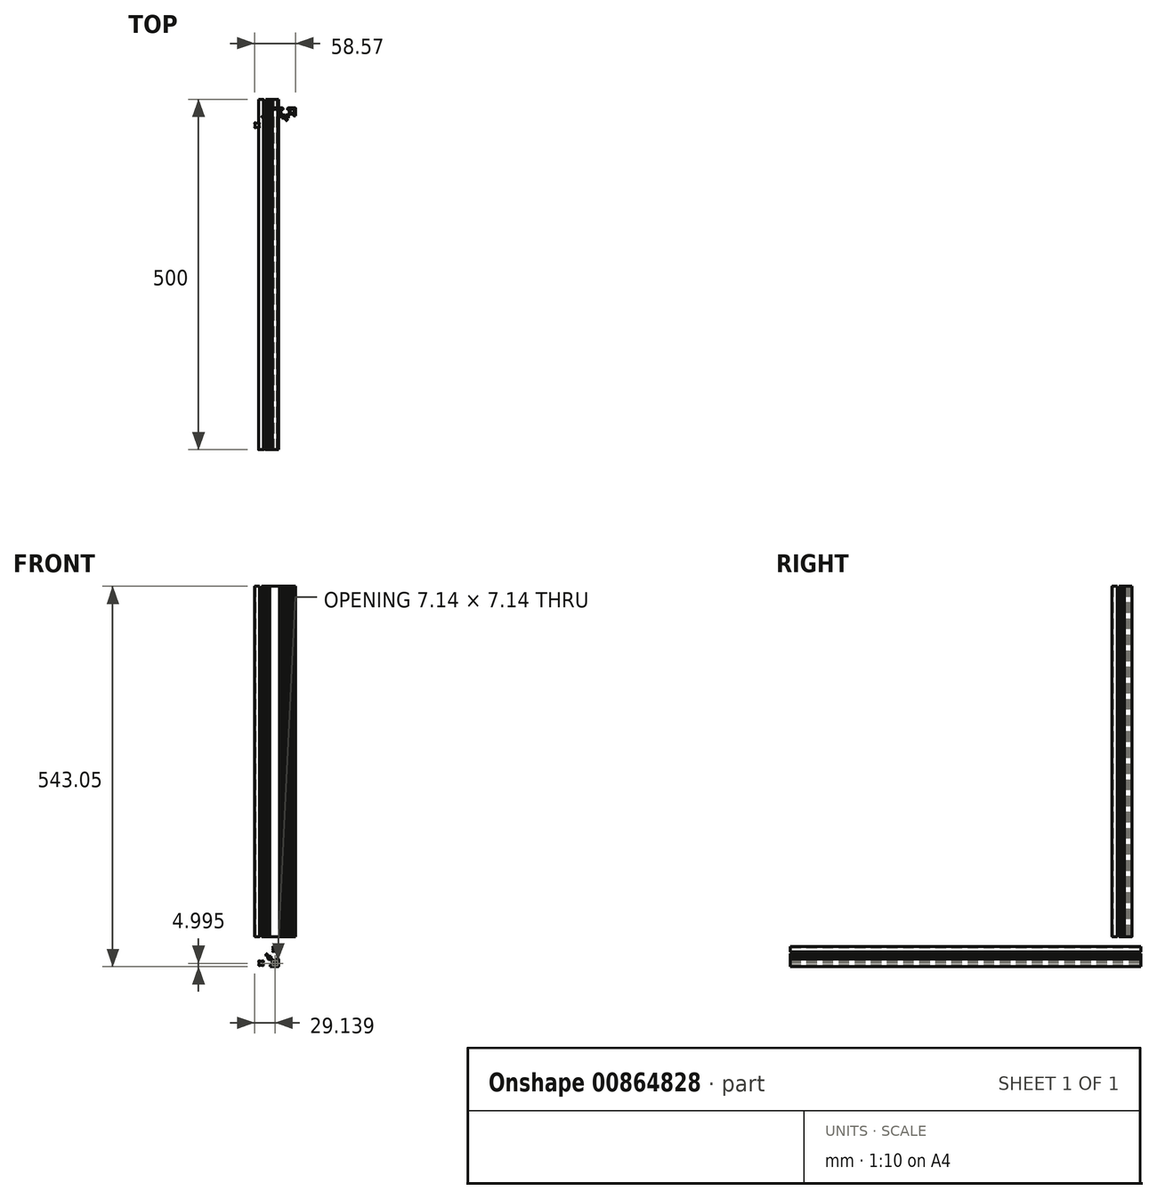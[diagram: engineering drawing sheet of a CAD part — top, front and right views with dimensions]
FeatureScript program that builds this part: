
annotation { "Feature Type Name" : "Feature", "Feature Type Description" : "" }
export const myFeature = defineFeature(function(context is Context, id is Id, definition is map)
    precondition{}
    {
        {
            var Q0;
            Q0=qCreatedBy(makeId("Top.planeOp"),FACE);
            var sketch = newSketch(context, id + "F0", { "sketchPlane" : qUnion([Q0])});
            skArc(sketch, "E0", {"start": v(-25.7, -35.74) * mm, "mid": v(-25.73, -35.56) * mm, "end": v(-25.65, -35.4) * mm});
            skLineSegment(sketch, "E1", {"start": v(-25.65, -35.4) * mm, "end": v(-24.9, -34.66) * mm});
            skArc(sketch, "E2", {"start": v(-24.9, -34.66) * mm, "mid": v(-24.82, -34.46) * mm, "end": v(-24.88, -34.26) * mm});
            skArc(sketch, "E3", {"start": v(-24.88, -34.26) * mm, "mid": v(-25.2, -33.9) * mm, "end": v(-25.57, -33.58) * mm});
            skArc(sketch, "E4", {"start": v(-25.57, -33.58) * mm, "mid": v(-25.77, -33.51) * mm, "end": v(-25.97, -33.6) * mm});
            skLineSegment(sketch, "E5", {"start": v(-25.97, -33.6) * mm, "end": v(-26.7, -34.34) * mm});
            skArc(sketch, "E6", {"start": v(-26.7, -34.34) * mm, "mid": v(-26.87, -34.42) * mm, "end": v(-27.05, -34.4) * mm});
            skArc(sketch, "E7", {"start": v(-27.05, -34.4) * mm, "mid": v(-28.39, -34.08) * mm, "end": v(-29.72, -34.4) * mm});
            skArc(sketch, "E8", {"start": v(-29.72, -34.4) * mm, "mid": v(-29.9, -34.42) * mm, "end": v(-30.07, -34.34) * mm});
            skLineSegment(sketch, "E9", {"start": v(-30.07, -34.34) * mm, "end": v(-30.81, -33.6) * mm});
            skArc(sketch, "E10", {"start": v(-30.81, -33.6) * mm, "mid": v(-31, -33.51) * mm, "end": v(-31.21, -33.58) * mm});
            skArc(sketch, "E11", {"start": v(-31.21, -33.58) * mm, "mid": v(-31.57, -33.9) * mm, "end": v(-31.9, -34.26) * mm});
            skArc(sketch, "E12", {"start": v(-31.9, -34.26) * mm, "mid": v(-31.96, -34.46) * mm, "end": v(-31.87, -34.66) * mm});
            skLineSegment(sketch, "E13", {"start": v(-31.87, -34.66) * mm, "end": v(-31.13, -35.4) * mm});
            skArc(sketch, "E14", {"start": v(-31.13, -35.4) * mm, "mid": v(-31.05, -35.56) * mm, "end": v(-31.07, -35.75) * mm});
            skArc(sketch, "E15", {"start": v(-31.07, -35.75) * mm, "mid": v(-31.39, -37.08) * mm, "end": v(-31.07, -38.42) * mm});
            skArc(sketch, "E16", {"start": v(-31.07, -38.42) * mm, "mid": v(-31.05, -38.6) * mm, "end": v(-31.13, -38.76) * mm});
            skLineSegment(sketch, "E17", {"start": v(-31.13, -38.76) * mm, "end": v(-31.87, -39.5) * mm});
            skArc(sketch, "E18", {"start": v(-31.87, -39.5) * mm, "mid": v(-31.96, -39.7) * mm, "end": v(-31.9, -39.9) * mm});
            skArc(sketch, "E19", {"start": v(-31.9, -39.9) * mm, "mid": v(-31.57, -40.26) * mm, "end": v(-31.21, -40.59) * mm});
            skArc(sketch, "E20", {"start": v(-31.21, -40.59) * mm, "mid": v(-31, -40.65) * mm, "end": v(-30.81, -40.56) * mm});
            skLineSegment(sketch, "E21", {"start": v(-30.81, -40.56) * mm, "end": v(-30.07, -39.82) * mm});
            skArc(sketch, "E22", {"start": v(-30.07, -39.82) * mm, "mid": v(-29.9, -39.74) * mm, "end": v(-29.72, -39.77) * mm});
            skArc(sketch, "E23", {"start": v(-29.72, -39.77) * mm, "mid": v(-28.39, -40.08) * mm, "end": v(-27.05, -39.77) * mm});
            skArc(sketch, "E24", {"start": v(-27.05, -39.77) * mm, "mid": v(-26.87, -39.74) * mm, "end": v(-26.7, -39.82) * mm});
            skLineSegment(sketch, "E25", {"start": v(-26.7, -39.82) * mm, "end": v(-25.97, -40.56) * mm});
            skArc(sketch, "E26", {"start": v(-25.97, -40.56) * mm, "mid": v(-25.77, -40.65) * mm, "end": v(-25.57, -40.59) * mm});
            skArc(sketch, "E27", {"start": v(-25.57, -40.59) * mm, "mid": v(-25.2, -40.26) * mm, "end": v(-24.88, -39.9) * mm});
            skArc(sketch, "E28", {"start": v(-24.88, -39.9) * mm, "mid": v(-24.82, -39.7) * mm, "end": v(-24.9, -39.5) * mm});
            skLineSegment(sketch, "E29", {"start": v(-24.9, -39.5) * mm, "end": v(-25.65, -38.76) * mm});
            skArc(sketch, "E30", {"start": v(-25.65, -38.76) * mm, "mid": v(-25.73, -38.6) * mm, "end": v(-25.7, -38.42) * mm});
            skArc(sketch, "E31", {"start": v(-25.7, -38.42) * mm, "mid": v(-25.39, -37.08) * mm, "end": v(-25.7, -35.74) * mm});
            skLineSegment(sketch, "E32", {"start": v(-28.39, -34.88) * mm, "end": v(-28.39, -39.28) * mm});
            skLineSegment(sketch, "E33", {"start": v(-26.19, -37.08) * mm, "end": v(-30.59, -37.08) * mm});
            skLineSegment(sketch, "E34", {"start": v(-26.19, -17.08) * mm, "end": v(-30.59, -17.08) * mm});
            skLineSegment(sketch, "E35", {"start": v(-28.39, -19.28) * mm, "end": v(-28.39, -14.88) * mm});
            skLineSegment(sketch, "E36", {"start": v(28.01, -27.08) * mm, "end": v(-34.9, -27.08) * mm});
            skLineSegment(sketch, "E37", {"start": v(-18.39, -43.65) * mm, "end": v(-18.39, -10.92) * mm});
            skArc(sketch, "E38", {"start": v(-15.15, -25.5) * mm, "mid": v(-14.93, -25.32) * mm, "end": v(-14.95, -25.05) * mm});
            skArc(sketch, "E39", {"start": v(-14.95, -25.05) * mm, "mid": v(-15.56, -24.25) * mm, "end": v(-16.36, -23.64) * mm});
            skArc(sketch, "E40", {"start": v(-16.36, -23.64) * mm, "mid": v(-16.63, -23.62) * mm, "end": v(-16.8, -23.84) * mm});
            skLineSegment(sketch, "E41", {"start": v(-16.8, -23.84) * mm, "end": v(-16.94, -24.58) * mm});
            skArc(sketch, "E42", {"start": v(-16.94, -24.58) * mm, "mid": v(-17.1, -24.8) * mm, "end": v(-17.36, -24.8) * mm});
            skArc(sketch, "E43", {"start": v(-17.36, -24.8) * mm, "mid": v(-18.39, -24.58) * mm, "end": v(-19.42, -24.8) * mm});
            skArc(sketch, "E44", {"start": v(-19.42, -24.8) * mm, "mid": v(-19.69, -24.8) * mm, "end": v(-19.84, -24.58) * mm});
            skLineSegment(sketch, "E45", {"start": v(-19.84, -24.58) * mm, "end": v(-19.98, -23.84) * mm});
            skArc(sketch, "E46", {"start": v(-19.98, -23.84) * mm, "mid": v(-20.15, -23.62) * mm, "end": v(-20.42, -23.64) * mm});
            skArc(sketch, "E47", {"start": v(-20.42, -23.64) * mm, "mid": v(-21.22, -24.25) * mm, "end": v(-21.83, -25.05) * mm});
            skArc(sketch, "E48", {"start": v(-21.83, -25.05) * mm, "mid": v(-21.85, -25.32) * mm, "end": v(-21.63, -25.5) * mm});
            skLineSegment(sketch, "E49", {"start": v(-21.63, -25.5) * mm, "end": v(-20.89, -25.63) * mm});
            skArc(sketch, "E50", {"start": v(-20.89, -25.63) * mm, "mid": v(-20.67, -25.78) * mm, "end": v(-20.67, -26.05) * mm});
            skArc(sketch, "E51", {"start": v(-20.67, -26.05) * mm, "mid": v(-20.89, -27.08) * mm, "end": v(-20.67, -28.11) * mm});
            skArc(sketch, "E52", {"start": v(-20.67, -28.11) * mm, "mid": v(-20.67, -28.38) * mm, "end": v(-20.89, -28.53) * mm});
            skLineSegment(sketch, "E53", {"start": v(-20.89, -28.53) * mm, "end": v(-21.63, -28.67) * mm});
            skArc(sketch, "E54", {"start": v(-21.63, -28.67) * mm, "mid": v(-21.85, -28.84) * mm, "end": v(-21.83, -29.11) * mm});
            skArc(sketch, "E55", {"start": v(-21.83, -29.11) * mm, "mid": v(-21.22, -29.9) * mm, "end": v(-20.42, -30.52) * mm});
            skArc(sketch, "E56", {"start": v(-20.42, -30.52) * mm, "mid": v(-20.15, -30.54) * mm, "end": v(-19.98, -30.32) * mm});
            skLineSegment(sketch, "E57", {"start": v(-19.98, -30.32) * mm, "end": v(-19.84, -29.58) * mm});
            skArc(sketch, "E58", {"start": v(-19.84, -29.58) * mm, "mid": v(-19.69, -29.36) * mm, "end": v(-19.42, -29.36) * mm});
            skArc(sketch, "E59", {"start": v(-19.42, -29.36) * mm, "mid": v(-18.39, -29.58) * mm, "end": v(-17.36, -29.36) * mm});
            skArc(sketch, "E60", {"start": v(-17.36, -29.36) * mm, "mid": v(-17.1, -29.36) * mm, "end": v(-16.94, -29.58) * mm});
            skLineSegment(sketch, "E61", {"start": v(-16.94, -29.58) * mm, "end": v(-16.8, -30.32) * mm});
            skArc(sketch, "E62", {"start": v(-16.8, -30.32) * mm, "mid": v(-16.63, -30.54) * mm, "end": v(-16.36, -30.52) * mm});
            skArc(sketch, "E63", {"start": v(-16.36, -30.52) * mm, "mid": v(-15.56, -29.9) * mm, "end": v(-14.95, -29.11) * mm});
            skArc(sketch, "E64", {"start": v(-14.95, -29.11) * mm, "mid": v(-14.93, -28.84) * mm, "end": v(-15.15, -28.67) * mm});
            skLineSegment(sketch, "E65", {"start": v(-15.15, -28.67) * mm, "end": v(-15.9, -28.53) * mm});
            skArc(sketch, "E66", {"start": v(-15.9, -28.53) * mm, "mid": v(-16.1, -28.38) * mm, "end": v(-16.11, -28.11) * mm});
            skArc(sketch, "E67", {"start": v(-16.11, -28.11) * mm, "mid": v(-15.89, -27.08) * mm, "end": v(-16.11, -26.05) * mm});
            skArc(sketch, "E68", {"start": v(-16.11, -26.05) * mm, "mid": v(-16.1, -25.78) * mm, "end": v(-15.9, -25.63) * mm});
            skLineSegment(sketch, "E69", {"start": v(-15.9, -25.63) * mm, "end": v(-15.15, -25.5) * mm});
            skArc(sketch, "E70", {"start": v(-25.7, -18.42) * mm, "mid": v(-25.73, -18.6) * mm, "end": v(-25.65, -18.76) * mm});
            skLineSegment(sketch, "E71", {"start": v(-25.65, -18.76) * mm, "end": v(-24.9, -19.5) * mm});
            skArc(sketch, "E72", {"start": v(-24.9, -19.5) * mm, "mid": v(-24.82, -19.7) * mm, "end": v(-24.88, -19.9) * mm});
            skArc(sketch, "E73", {"start": v(-24.88, -19.9) * mm, "mid": v(-25.2, -20.26) * mm, "end": v(-25.57, -20.59) * mm});
            skArc(sketch, "E74", {"start": v(-25.57, -20.59) * mm, "mid": v(-25.77, -20.65) * mm, "end": v(-25.97, -20.56) * mm});
            skLineSegment(sketch, "E75", {"start": v(-25.97, -20.56) * mm, "end": v(-26.7, -19.82) * mm});
            skArc(sketch, "E76", {"start": v(-26.7, -19.82) * mm, "mid": v(-26.87, -19.74) * mm, "end": v(-27.05, -19.77) * mm});
            skArc(sketch, "E77", {"start": v(-27.05, -19.77) * mm, "mid": v(-28.39, -20.08) * mm, "end": v(-29.73, -19.77) * mm});
            skArc(sketch, "E78", {"start": v(-29.73, -19.77) * mm, "mid": v(-29.9, -19.74) * mm, "end": v(-30.07, -19.82) * mm});
            skLineSegment(sketch, "E79", {"start": v(-30.07, -19.82) * mm, "end": v(-30.81, -20.56) * mm});
            skArc(sketch, "E80", {"start": v(-30.81, -20.56) * mm, "mid": v(-31, -20.65) * mm, "end": v(-31.21, -20.59) * mm});
            skArc(sketch, "E81", {"start": v(-31.21, -20.59) * mm, "mid": v(-31.57, -20.26) * mm, "end": v(-31.9, -19.9) * mm});
            skArc(sketch, "E82", {"start": v(-31.9, -19.9) * mm, "mid": v(-31.96, -19.7) * mm, "end": v(-31.87, -19.5) * mm});
            skLineSegment(sketch, "E83", {"start": v(-31.87, -19.5) * mm, "end": v(-31.13, -18.76) * mm});
            skArc(sketch, "E84", {"start": v(-31.13, -18.76) * mm, "mid": v(-31.05, -18.6) * mm, "end": v(-31.08, -18.42) * mm});
            skArc(sketch, "E85", {"start": v(-31.08, -18.42) * mm, "mid": v(-31.39, -17.08) * mm, "end": v(-31.08, -15.74) * mm});
            skArc(sketch, "E86", {"start": v(-31.08, -15.74) * mm, "mid": v(-31.05, -15.56) * mm, "end": v(-31.13, -15.4) * mm});
            skLineSegment(sketch, "E87", {"start": v(-31.13, -15.4) * mm, "end": v(-31.87, -14.66) * mm});
            skArc(sketch, "E88", {"start": v(-31.87, -14.66) * mm, "mid": v(-31.96, -14.46) * mm, "end": v(-31.9, -14.26) * mm});
            skArc(sketch, "E89", {"start": v(-31.9, -14.26) * mm, "mid": v(-31.57, -13.9) * mm, "end": v(-31.21, -13.58) * mm});
            skArc(sketch, "E90", {"start": v(-31.21, -13.58) * mm, "mid": v(-31, -13.5) * mm, "end": v(-30.81, -13.6) * mm});
            skLineSegment(sketch, "E91", {"start": v(-30.81, -13.6) * mm, "end": v(-30.07, -14.34) * mm});
            skArc(sketch, "E92", {"start": v(-30.07, -14.34) * mm, "mid": v(-29.9, -14.42) * mm, "end": v(-29.73, -14.4) * mm});
            skArc(sketch, "E93", {"start": v(-29.73, -14.4) * mm, "mid": v(-28.39, -14.08) * mm, "end": v(-27.05, -14.4) * mm});
            skArc(sketch, "E94", {"start": v(-27.05, -14.4) * mm, "mid": v(-26.87, -14.42) * mm, "end": v(-26.7, -14.34) * mm});
            skLineSegment(sketch, "E95", {"start": v(-26.7, -14.34) * mm, "end": v(-25.97, -13.6) * mm});
            skArc(sketch, "E96", {"start": v(-25.97, -13.6) * mm, "mid": v(-25.77, -13.5) * mm, "end": v(-25.57, -13.58) * mm});
            skArc(sketch, "E97", {"start": v(-25.57, -13.58) * mm, "mid": v(-25.2, -13.9) * mm, "end": v(-24.88, -14.26) * mm});
            skArc(sketch, "E98", {"start": v(-24.88, -14.26) * mm, "mid": v(-24.82, -14.46) * mm, "end": v(-24.9, -14.66) * mm});
            skLineSegment(sketch, "E99", {"start": v(-24.9, -14.66) * mm, "end": v(-25.65, -15.4) * mm});
            skArc(sketch, "E100", {"start": v(-25.65, -15.4) * mm, "mid": v(-25.73, -15.56) * mm, "end": v(-25.7, -15.74) * mm});
            skArc(sketch, "E101", {"start": v(-25.7, -15.74) * mm, "mid": v(-25.39, -17.08) * mm, "end": v(-25.7, -18.42) * mm});
            skLineSegment(sketch, "E102", {"start": v(-13.38, -27.08) * mm, "end": v(-12.88, -27.08) * mm});
            skArc(sketch, "E103", {"start": v(14.85, -25.5) * mm, "mid": v(15.07, -25.32) * mm, "end": v(15.05, -25.05) * mm});
            skArc(sketch, "E104", {"start": v(15.05, -25.05) * mm, "mid": v(14.44, -24.25) * mm, "end": v(13.64, -23.64) * mm});
            skArc(sketch, "E105", {"start": v(13.64, -23.64) * mm, "mid": v(13.37, -23.62) * mm, "end": v(13.2, -23.84) * mm});
            skLineSegment(sketch, "E106", {"start": v(13.2, -23.84) * mm, "end": v(13.06, -24.58) * mm});
            skArc(sketch, "E107", {"start": v(13.06, -24.58) * mm, "mid": v(12.9, -24.8) * mm, "end": v(12.64, -24.8) * mm});
            skArc(sketch, "E108", {"start": v(12.64, -24.8) * mm, "mid": v(11.61, -24.58) * mm, "end": v(10.58, -24.8) * mm});
            skArc(sketch, "E109", {"start": v(10.58, -24.8) * mm, "mid": v(10.31, -24.8) * mm, "end": v(10.16, -24.58) * mm});
            skLineSegment(sketch, "E110", {"start": v(10.16, -24.58) * mm, "end": v(10.02, -23.84) * mm});
            skArc(sketch, "E111", {"start": v(10.02, -23.84) * mm, "mid": v(9.85, -23.62) * mm, "end": v(9.58, -23.64) * mm});
            skArc(sketch, "E112", {"start": v(9.58, -23.64) * mm, "mid": v(8.78, -24.25) * mm, "end": v(8.17, -25.05) * mm});
            skArc(sketch, "E113", {"start": v(8.17, -25.05) * mm, "mid": v(8.15, -25.32) * mm, "end": v(8.37, -25.5) * mm});
            skLineSegment(sketch, "E114", {"start": v(8.37, -25.5) * mm, "end": v(9.11, -25.63) * mm});
            skArc(sketch, "E115", {"start": v(9.11, -25.63) * mm, "mid": v(9.33, -25.78) * mm, "end": v(9.33, -26.05) * mm});
            skArc(sketch, "E116", {"start": v(9.33, -26.05) * mm, "mid": v(9.11, -27.08) * mm, "end": v(9.33, -28.11) * mm});
            skArc(sketch, "E117", {"start": v(9.33, -28.11) * mm, "mid": v(9.33, -28.38) * mm, "end": v(9.11, -28.53) * mm});
            skLineSegment(sketch, "E118", {"start": v(9.11, -28.53) * mm, "end": v(8.37, -28.67) * mm});
            skArc(sketch, "E119", {"start": v(8.37, -28.67) * mm, "mid": v(8.15, -28.84) * mm, "end": v(8.17, -29.11) * mm});
            skArc(sketch, "E120", {"start": v(8.17, -29.11) * mm, "mid": v(8.78, -29.9) * mm, "end": v(9.58, -30.52) * mm});
            skArc(sketch, "E121", {"start": v(9.58, -30.52) * mm, "mid": v(9.85, -30.54) * mm, "end": v(10.02, -30.32) * mm});
            skLineSegment(sketch, "E122", {"start": v(10.02, -30.32) * mm, "end": v(10.16, -29.58) * mm});
            skArc(sketch, "E123", {"start": v(10.16, -29.58) * mm, "mid": v(10.31, -29.36) * mm, "end": v(10.58, -29.36) * mm});
            skArc(sketch, "E124", {"start": v(10.58, -29.36) * mm, "mid": v(11.61, -29.58) * mm, "end": v(12.64, -29.36) * mm});
            skArc(sketch, "E125", {"start": v(12.64, -29.36) * mm, "mid": v(12.9, -29.36) * mm, "end": v(13.06, -29.58) * mm});
            skLineSegment(sketch, "E126", {"start": v(13.06, -29.58) * mm, "end": v(13.2, -30.32) * mm});
            skArc(sketch, "E127", {"start": v(13.2, -30.32) * mm, "mid": v(13.37, -30.54) * mm, "end": v(13.64, -30.52) * mm});
            skArc(sketch, "E128", {"start": v(13.64, -30.52) * mm, "mid": v(14.44, -29.9) * mm, "end": v(15.05, -29.11) * mm});
            skArc(sketch, "E129", {"start": v(15.05, -29.11) * mm, "mid": v(15.07, -28.84) * mm, "end": v(14.85, -28.67) * mm});
            skLineSegment(sketch, "E130", {"start": v(14.85, -28.67) * mm, "end": v(14.1, -28.53) * mm});
            skArc(sketch, "E131", {"start": v(14.1, -28.53) * mm, "mid": v(13.9, -28.38) * mm, "end": v(13.89, -28.11) * mm});
            skArc(sketch, "E132", {"start": v(13.89, -28.11) * mm, "mid": v(14.11, -27.08) * mm, "end": v(13.89, -26.05) * mm});
            skArc(sketch, "E133", {"start": v(13.89, -26.05) * mm, "mid": v(13.9, -25.78) * mm, "end": v(14.1, -25.63) * mm});
            skLineSegment(sketch, "E134", {"start": v(14.1, -25.63) * mm, "end": v(14.85, -25.5) * mm});
            skArc(sketch, "E135", {"start": v(18.92, -35.74) * mm, "mid": v(18.95, -35.56) * mm, "end": v(18.87, -35.4) * mm});
            skLineSegment(sketch, "E136", {"start": v(18.87, -35.4) * mm, "end": v(18.12, -34.66) * mm});
            skArc(sketch, "E137", {"start": v(18.12, -34.66) * mm, "mid": v(18.04, -34.46) * mm, "end": v(18.1, -34.26) * mm});
            skArc(sketch, "E138", {"start": v(18.1, -34.26) * mm, "mid": v(18.43, -33.9) * mm, "end": v(18.79, -33.58) * mm});
            skArc(sketch, "E139", {"start": v(18.79, -33.58) * mm, "mid": v(18.99, -33.51) * mm, "end": v(19.19, -33.6) * mm});
            skLineSegment(sketch, "E140", {"start": v(19.19, -33.6) * mm, "end": v(19.93, -34.34) * mm});
            skArc(sketch, "E141", {"start": v(19.93, -34.34) * mm, "mid": v(20.09, -34.42) * mm, "end": v(20.27, -34.4) * mm});
            skArc(sketch, "E142", {"start": v(20.27, -34.4) * mm, "mid": v(21.6, -34.08) * mm, "end": v(22.94, -34.4) * mm});
            skArc(sketch, "E143", {"start": v(22.94, -34.4) * mm, "mid": v(23.13, -34.42) * mm, "end": v(23.29, -34.34) * mm});
            skLineSegment(sketch, "E144", {"start": v(23.29, -34.34) * mm, "end": v(24.03, -33.6) * mm});
            skArc(sketch, "E145", {"start": v(24.03, -33.6) * mm, "mid": v(24.23, -33.51) * mm, "end": v(24.43, -33.58) * mm});
            skArc(sketch, "E146", {"start": v(24.43, -33.58) * mm, "mid": v(24.79, -33.9) * mm, "end": v(25.11, -34.26) * mm});
            skArc(sketch, "E147", {"start": v(25.11, -34.26) * mm, "mid": v(25.18, -34.46) * mm, "end": v(25.1, -34.66) * mm});
            skLineSegment(sketch, "E148", {"start": v(25.1, -34.66) * mm, "end": v(24.35, -35.4) * mm});
            skArc(sketch, "E149", {"start": v(24.35, -35.4) * mm, "mid": v(24.27, -35.56) * mm, "end": v(24.3, -35.75) * mm});
            skArc(sketch, "E150", {"start": v(24.3, -35.75) * mm, "mid": v(24.6, -37.08) * mm, "end": v(24.3, -38.42) * mm});
            skArc(sketch, "E151", {"start": v(24.3, -38.42) * mm, "mid": v(24.27, -38.6) * mm, "end": v(24.35, -38.76) * mm});
            skLineSegment(sketch, "E152", {"start": v(24.35, -38.76) * mm, "end": v(25.1, -39.5) * mm});
            skArc(sketch, "E153", {"start": v(25.1, -39.5) * mm, "mid": v(25.18, -39.7) * mm, "end": v(25.11, -39.9) * mm});
            skArc(sketch, "E154", {"start": v(25.11, -39.9) * mm, "mid": v(24.79, -40.26) * mm, "end": v(24.43, -40.59) * mm});
            skArc(sketch, "E155", {"start": v(24.43, -40.59) * mm, "mid": v(24.23, -40.65) * mm, "end": v(24.03, -40.56) * mm});
            skLineSegment(sketch, "E156", {"start": v(24.03, -40.56) * mm, "end": v(23.29, -39.82) * mm});
            skArc(sketch, "E157", {"start": v(23.29, -39.82) * mm, "mid": v(23.13, -39.74) * mm, "end": v(22.94, -39.77) * mm});
            skArc(sketch, "E158", {"start": v(22.94, -39.77) * mm, "mid": v(21.6, -40.08) * mm, "end": v(20.27, -39.77) * mm});
            skArc(sketch, "E159", {"start": v(20.27, -39.77) * mm, "mid": v(20.09, -39.74) * mm, "end": v(19.93, -39.82) * mm});
            skLineSegment(sketch, "E160", {"start": v(19.93, -39.82) * mm, "end": v(19.18, -40.56) * mm});
            skArc(sketch, "E161", {"start": v(19.18, -40.56) * mm, "mid": v(18.99, -40.65) * mm, "end": v(18.78, -40.59) * mm});
            skArc(sketch, "E162", {"start": v(18.78, -40.59) * mm, "mid": v(18.43, -40.26) * mm, "end": v(18.1, -39.9) * mm});
            skArc(sketch, "E163", {"start": v(18.1, -39.9) * mm, "mid": v(18.04, -39.7) * mm, "end": v(18.12, -39.5) * mm});
            skLineSegment(sketch, "E164", {"start": v(18.12, -39.5) * mm, "end": v(18.86, -38.76) * mm});
            skArc(sketch, "E165", {"start": v(18.86, -38.76) * mm, "mid": v(18.95, -38.6) * mm, "end": v(18.92, -38.42) * mm});
            skArc(sketch, "E166", {"start": v(18.92, -38.42) * mm, "mid": v(18.6, -37.08) * mm, "end": v(18.92, -35.74) * mm});
            skLineSegment(sketch, "E167", {"start": v(21.6, -34.88) * mm, "end": v(21.6, -39.28) * mm});
            skLineSegment(sketch, "E168", {"start": v(19.4, -37.08) * mm, "end": v(23.8, -37.08) * mm});
            skArc(sketch, "E169", {"start": v(18.92, -18.42) * mm, "mid": v(18.95, -18.6) * mm, "end": v(18.87, -18.76) * mm});
            skLineSegment(sketch, "E170", {"start": v(18.87, -18.76) * mm, "end": v(18.13, -19.5) * mm});
            skArc(sketch, "E171", {"start": v(18.13, -19.5) * mm, "mid": v(18.04, -19.7) * mm, "end": v(18.1, -19.9) * mm});
            skArc(sketch, "E172", {"start": v(18.1, -19.9) * mm, "mid": v(18.43, -20.26) * mm, "end": v(18.79, -20.59) * mm});
            skArc(sketch, "E173", {"start": v(18.79, -20.59) * mm, "mid": v(18.99, -20.65) * mm, "end": v(19.19, -20.56) * mm});
            skLineSegment(sketch, "E174", {"start": v(19.19, -20.56) * mm, "end": v(19.93, -19.82) * mm});
            skArc(sketch, "E175", {"start": v(19.93, -19.82) * mm, "mid": v(20.1, -19.74) * mm, "end": v(20.27, -19.77) * mm});
            skArc(sketch, "E176", {"start": v(20.27, -19.77) * mm, "mid": v(21.6, -20.08) * mm, "end": v(22.94, -19.77) * mm});
            skArc(sketch, "E177", {"start": v(22.94, -19.77) * mm, "mid": v(23.13, -19.74) * mm, "end": v(23.3, -19.82) * mm});
            skLineSegment(sketch, "E178", {"start": v(23.3, -19.82) * mm, "end": v(24.03, -20.56) * mm});
            skArc(sketch, "E179", {"start": v(24.03, -20.56) * mm, "mid": v(24.23, -20.65) * mm, "end": v(24.43, -20.59) * mm});
            skArc(sketch, "E180", {"start": v(24.43, -20.59) * mm, "mid": v(24.8, -20.26) * mm, "end": v(25.11, -19.9) * mm});
            skArc(sketch, "E181", {"start": v(25.11, -19.9) * mm, "mid": v(25.18, -19.7) * mm, "end": v(25.1, -19.5) * mm});
            skLineSegment(sketch, "E182", {"start": v(25.1, -19.5) * mm, "end": v(24.35, -18.76) * mm});
            skArc(sketch, "E183", {"start": v(24.35, -18.76) * mm, "mid": v(24.27, -18.6) * mm, "end": v(24.3, -18.42) * mm});
            skArc(sketch, "E184", {"start": v(24.3, -18.42) * mm, "mid": v(24.6, -17.08) * mm, "end": v(24.3, -15.74) * mm});
            skArc(sketch, "E185", {"start": v(24.3, -15.74) * mm, "mid": v(24.27, -15.56) * mm, "end": v(24.35, -15.4) * mm});
            skLineSegment(sketch, "E186", {"start": v(24.35, -15.4) * mm, "end": v(25.1, -14.66) * mm});
            skArc(sketch, "E187", {"start": v(25.1, -14.66) * mm, "mid": v(25.18, -14.46) * mm, "end": v(25.11, -14.26) * mm});
            skArc(sketch, "E188", {"start": v(25.11, -14.26) * mm, "mid": v(24.8, -13.9) * mm, "end": v(24.43, -13.58) * mm});
            skArc(sketch, "E189", {"start": v(24.43, -13.58) * mm, "mid": v(24.23, -13.5) * mm, "end": v(24.03, -13.6) * mm});
            skLineSegment(sketch, "E190", {"start": v(24.03, -13.6) * mm, "end": v(23.3, -14.34) * mm});
            skArc(sketch, "E191", {"start": v(23.3, -14.34) * mm, "mid": v(23.13, -14.42) * mm, "end": v(22.94, -14.4) * mm});
            skArc(sketch, "E192", {"start": v(22.94, -14.4) * mm, "mid": v(21.6, -14.08) * mm, "end": v(20.27, -14.4) * mm});
            skArc(sketch, "E193", {"start": v(20.27, -14.4) * mm, "mid": v(20.1, -14.42) * mm, "end": v(19.93, -14.34) * mm});
            skLineSegment(sketch, "E194", {"start": v(19.93, -14.34) * mm, "end": v(19.19, -13.6) * mm});
            skArc(sketch, "E195", {"start": v(19.19, -13.6) * mm, "mid": v(18.99, -13.5) * mm, "end": v(18.79, -13.58) * mm});
            skArc(sketch, "E196", {"start": v(18.79, -13.58) * mm, "mid": v(18.43, -13.9) * mm, "end": v(18.1, -14.26) * mm});
            skArc(sketch, "E197", {"start": v(18.1, -14.26) * mm, "mid": v(18.04, -14.46) * mm, "end": v(18.13, -14.66) * mm});
            skLineSegment(sketch, "E198", {"start": v(18.13, -14.66) * mm, "end": v(18.87, -15.4) * mm});
            skArc(sketch, "E199", {"start": v(18.87, -15.4) * mm, "mid": v(18.95, -15.56) * mm, "end": v(18.92, -15.74) * mm});
            skArc(sketch, "E200", {"start": v(18.92, -15.74) * mm, "mid": v(18.6, -17.08) * mm, "end": v(18.92, -18.42) * mm});
            skLineSegment(sketch, "E201", {"start": v(19.4, -17.08) * mm, "end": v(23.8, -17.08) * mm});
            skLineSegment(sketch, "E202", {"start": v(21.6, -19.28) * mm, "end": v(21.6, -14.88) * mm});
            skLineSegment(sketch, "E203", {"start": v(6.6, -27.08) * mm, "end": v(6.1, -27.08) * mm});
            skLineSegment(sketch, "E204", {"start": v(4.69, -20.81) * mm, "end": v(6.48, -22.73) * mm});
            skArc(sketch, "E205", {"start": v(6.48, -22.73) * mm, "mid": v(6.58, -22.88) * mm, "end": v(6.61, -23.07) * mm});
            skLineSegment(sketch, "E206", {"start": v(6.61, -23.07) * mm, "end": v(6.61, -26.58) * mm});
            skLineSegment(sketch, "E207", {"start": v(6.61, -26.58) * mm, "end": v(7.11, -27.08) * mm});
            skLineSegment(sketch, "E208", {"start": v(7.11, -27.08) * mm, "end": v(6.61, -27.58) * mm});
            skLineSegment(sketch, "E209", {"start": v(6.61, -27.58) * mm, "end": v(6.61, -31.1) * mm});
            skArc(sketch, "E210", {"start": v(6.61, -31.1) * mm, "mid": v(6.58, -31.28) * mm, "end": v(6.48, -31.44) * mm});
            skLineSegment(sketch, "E211", {"start": v(6.48, -31.44) * mm, "end": v(4.69, -33.35) * mm});
            skArc(sketch, "E212", {"start": v(4.69, -33.35) * mm, "mid": v(3.7, -35.22) * mm, "end": v(3.81, -37.34) * mm});
            skLineSegment(sketch, "E213", {"start": v(3.81, -37.34) * mm, "end": v(4.76, -39.37) * mm});
            skArc(sketch, "E214", {"start": v(4.76, -39.37) * mm, "mid": v(4.73, -39.85) * mm, "end": v(4.3, -40.08) * mm});
            skLineSegment(sketch, "E215", {"start": v(4.3, -40.08) * mm, "end": v(-11.08, -40.08) * mm});
            skArc(sketch, "E216", {"start": v(-11.08, -40.08) * mm, "mid": v(-11.5, -39.85) * mm, "end": v(-11.54, -39.37) * mm});
            skLineSegment(sketch, "E217", {"start": v(-11.54, -39.37) * mm, "end": v(-10.6, -37.34) * mm});
            skArc(sketch, "E218", {"start": v(-10.6, -37.34) * mm, "mid": v(-10.48, -35.22) * mm, "end": v(-11.47, -33.35) * mm});
            skLineSegment(sketch, "E219", {"start": v(-11.47, -33.35) * mm, "end": v(-13.25, -31.44) * mm});
            skArc(sketch, "E220", {"start": v(-13.25, -31.44) * mm, "mid": v(-13.35, -31.28) * mm, "end": v(-13.39, -31.1) * mm});
            skLineSegment(sketch, "E221", {"start": v(-13.39, -31.1) * mm, "end": v(-13.39, -27.58) * mm});
            skLineSegment(sketch, "E222", {"start": v(-13.39, -27.58) * mm, "end": v(-13.89, -27.08) * mm});
            skLineSegment(sketch, "E223", {"start": v(-13.89, -27.08) * mm, "end": v(-13.39, -26.58) * mm});
            skLineSegment(sketch, "E224", {"start": v(-13.39, -26.58) * mm, "end": v(-13.39, -23.07) * mm});
            skArc(sketch, "E225", {"start": v(-13.39, -23.07) * mm, "mid": v(-13.35, -22.88) * mm, "end": v(-13.25, -22.73) * mm});
            skLineSegment(sketch, "E226", {"start": v(-13.25, -22.73) * mm, "end": v(-11.47, -20.81) * mm});
            skArc(sketch, "E227", {"start": v(-11.47, -20.81) * mm, "mid": v(-10.48, -18.94) * mm, "end": v(-10.6, -16.82) * mm});
            skLineSegment(sketch, "E228", {"start": v(-10.6, -16.82) * mm, "end": v(-11.54, -14.8) * mm});
            skArc(sketch, "E229", {"start": v(-11.54, -14.8) * mm, "mid": v(-11.5, -14.31) * mm, "end": v(-11.08, -14.08) * mm});
            skLineSegment(sketch, "E230", {"start": v(-11.08, -14.08) * mm, "end": v(4.3, -14.08) * mm});
            skArc(sketch, "E231", {"start": v(4.3, -14.08) * mm, "mid": v(4.73, -14.31) * mm, "end": v(4.76, -14.8) * mm});
            skLineSegment(sketch, "E232", {"start": v(4.76, -14.8) * mm, "end": v(3.81, -16.82) * mm});
            skArc(sketch, "E233", {"start": v(3.81, -16.82) * mm, "mid": v(3.7, -18.94) * mm, "end": v(4.69, -20.81) * mm});
            skLineSegment(sketch, "E234", {"start": v(11.61, -43.65) * mm, "end": v(11.61, -10.92) * mm});
            skLineSegment(sketch, "E235", {"start": v(-14.44, -42.08) * mm, "end": v(7.66, -42.08) * mm});
            skLineSegment(sketch, "E236", {"start": v(7.66, -42.08) * mm, "end": v(8.46, -41.58) * mm});
            skLineSegment(sketch, "E237", {"start": v(8.46, -41.58) * mm, "end": v(8.46, -39.88) * mm});
            skArc(sketch, "E238", {"start": v(8.46, -39.88) * mm, "mid": v(8.37, -39.67) * mm, "end": v(8.16, -39.58) * mm});
            skLineSegment(sketch, "E239", {"start": v(8.16, -39.58) * mm, "end": v(6.51, -39.58) * mm});
            skLineSegment(sketch, "E240", {"start": v(6.51, -39.58) * mm, "end": v(5.52, -36.53) * mm});
            skArc(sketch, "E241", {"start": v(5.52, -36.53) * mm, "mid": v(5.48, -36.27) * mm, "end": v(5.5, -36) * mm});
            skArc(sketch, "E242", {"start": v(5.5, -36) * mm, "mid": v(6.34, -33.97) * mm, "end": v(7.6, -32.17) * mm});
            skArc(sketch, "E243", {"start": v(7.6, -32.17) * mm, "mid": v(8.45, -31.73) * mm, "end": v(9.4, -31.58) * mm});
            skLineSegment(sketch, "E244", {"start": v(9.4, -31.58) * mm, "end": v(11.11, -31.58) * mm});
            skLineSegment(sketch, "E245", {"start": v(11.11, -31.58) * mm, "end": v(11.61, -31.08) * mm});
            skLineSegment(sketch, "E246", {"start": v(11.61, -31.08) * mm, "end": v(12.11, -31.58) * mm});
            skLineSegment(sketch, "E247", {"start": v(12.11, -31.58) * mm, "end": v(13.83, -31.58) * mm});
            skArc(sketch, "E248", {"start": v(13.83, -31.58) * mm, "mid": v(14.77, -31.73) * mm, "end": v(15.61, -32.17) * mm});
            skArc(sketch, "E249", {"start": v(15.61, -32.17) * mm, "mid": v(16.89, -33.97) * mm, "end": v(17.72, -36) * mm});
            skArc(sketch, "E250", {"start": v(17.72, -36) * mm, "mid": v(17.75, -36.27) * mm, "end": v(17.7, -36.53) * mm});
            skLineSegment(sketch, "E251", {"start": v(17.7, -36.53) * mm, "end": v(16.71, -39.58) * mm});
            skLineSegment(sketch, "E252", {"start": v(16.71, -39.58) * mm, "end": v(15.06, -39.58) * mm});
            skArc(sketch, "E253", {"start": v(15.06, -39.58) * mm, "mid": v(14.85, -39.67) * mm, "end": v(14.76, -39.88) * mm});
            skLineSegment(sketch, "E254", {"start": v(14.76, -39.88) * mm, "end": v(14.76, -41.58) * mm});
            skLineSegment(sketch, "E255", {"start": v(14.76, -41.58) * mm, "end": v(15.56, -42.08) * mm});
            skLineSegment(sketch, "E256", {"start": v(15.56, -42.08) * mm, "end": v(25.61, -42.08) * mm});
            skArc(sketch, "E257", {"start": v(25.61, -42.08) * mm, "mid": v(26.32, -41.79) * mm, "end": v(26.61, -41.08) * mm});
            skLineSegment(sketch, "E258", {"start": v(26.61, -41.08) * mm, "end": v(26.61, -31.03) * mm});
            skLineSegment(sketch, "E259", {"start": v(26.61, -31.03) * mm, "end": v(26.11, -30.23) * mm});
            skLineSegment(sketch, "E260", {"start": v(26.11, -30.23) * mm, "end": v(24.41, -30.23) * mm});
            skArc(sketch, "E261", {"start": v(24.41, -30.23) * mm, "mid": v(24.2, -30.32) * mm, "end": v(24.11, -30.53) * mm});
            skLineSegment(sketch, "E262", {"start": v(24.11, -30.53) * mm, "end": v(24.11, -32.18) * mm});
            skLineSegment(sketch, "E263", {"start": v(24.11, -32.18) * mm, "end": v(21.06, -33.17) * mm});
            skArc(sketch, "E264", {"start": v(21.06, -33.17) * mm, "mid": v(20.8, -33.22) * mm, "end": v(20.54, -33.2) * mm});
            skArc(sketch, "E265", {"start": v(20.54, -33.2) * mm, "mid": v(18.5, -32.36) * mm, "end": v(16.7, -31.08) * mm});
            skArc(sketch, "E266", {"start": v(16.7, -31.08) * mm, "mid": v(16.26, -30.24) * mm, "end": v(16.11, -29.3) * mm});
            skLineSegment(sketch, "E267", {"start": v(16.11, -29.3) * mm, "end": v(16.11, -27.58) * mm});
            skLineSegment(sketch, "E268", {"start": v(16.11, -27.58) * mm, "end": v(15.61, -27.08) * mm});
            skLineSegment(sketch, "E269", {"start": v(15.61, -27.08) * mm, "end": v(16.11, -26.58) * mm});
            skLineSegment(sketch, "E270", {"start": v(16.11, -26.58) * mm, "end": v(16.11, -24.86) * mm});
            skArc(sketch, "E271", {"start": v(16.11, -24.86) * mm, "mid": v(16.26, -23.92) * mm, "end": v(16.7, -23.08) * mm});
            skArc(sketch, "E272", {"start": v(16.7, -23.08) * mm, "mid": v(18.5, -21.8) * mm, "end": v(20.54, -20.97) * mm});
            skArc(sketch, "E273", {"start": v(20.54, -20.97) * mm, "mid": v(20.8, -20.95) * mm, "end": v(21.06, -21) * mm});
            skLineSegment(sketch, "E274", {"start": v(21.06, -21) * mm, "end": v(24.11, -21.98) * mm});
            skLineSegment(sketch, "E275", {"start": v(24.11, -21.98) * mm, "end": v(24.11, -23.63) * mm});
            skArc(sketch, "E276", {"start": v(24.11, -23.63) * mm, "mid": v(24.2, -23.84) * mm, "end": v(24.41, -23.93) * mm});
            skLineSegment(sketch, "E277", {"start": v(24.41, -23.93) * mm, "end": v(26.11, -23.93) * mm});
            skLineSegment(sketch, "E278", {"start": v(26.11, -23.93) * mm, "end": v(26.61, -23.13) * mm});
            skLineSegment(sketch, "E279", {"start": v(26.61, -23.13) * mm, "end": v(26.61, -13.08) * mm});
            skArc(sketch, "E280", {"start": v(26.61, -13.08) * mm, "mid": v(26.32, -12.37) * mm, "end": v(25.61, -12.08) * mm});
            skLineSegment(sketch, "E281", {"start": v(25.61, -12.08) * mm, "end": v(15.56, -12.08) * mm});
            skLineSegment(sketch, "E282", {"start": v(15.56, -12.08) * mm, "end": v(14.76, -12.58) * mm});
            skLineSegment(sketch, "E283", {"start": v(14.76, -12.58) * mm, "end": v(14.76, -14.28) * mm});
            skArc(sketch, "E284", {"start": v(14.76, -14.28) * mm, "mid": v(14.85, -14.5) * mm, "end": v(15.06, -14.58) * mm});
            skLineSegment(sketch, "E285", {"start": v(15.06, -14.58) * mm, "end": v(16.71, -14.58) * mm});
            skLineSegment(sketch, "E286", {"start": v(16.71, -14.58) * mm, "end": v(17.7, -17.63) * mm});
            skArc(sketch, "E287", {"start": v(17.7, -17.63) * mm, "mid": v(17.75, -17.9) * mm, "end": v(17.72, -18.15) * mm});
            skArc(sketch, "E288", {"start": v(17.72, -18.15) * mm, "mid": v(16.89, -20.2) * mm, "end": v(15.61, -22) * mm});
            skArc(sketch, "E289", {"start": v(15.61, -22) * mm, "mid": v(14.77, -22.43) * mm, "end": v(13.83, -22.58) * mm});
            skLineSegment(sketch, "E290", {"start": v(13.83, -22.58) * mm, "end": v(12.11, -22.58) * mm});
            skLineSegment(sketch, "E291", {"start": v(12.11, -22.58) * mm, "end": v(11.61, -23.08) * mm});
            skLineSegment(sketch, "E292", {"start": v(11.61, -23.08) * mm, "end": v(11.11, -22.58) * mm});
            skLineSegment(sketch, "E293", {"start": v(11.11, -22.58) * mm, "end": v(9.4, -22.58) * mm});
            skArc(sketch, "E294", {"start": v(9.4, -22.58) * mm, "mid": v(8.45, -22.43) * mm, "end": v(7.6, -22) * mm});
            skArc(sketch, "E295", {"start": v(7.6, -22) * mm, "mid": v(6.34, -20.2) * mm, "end": v(5.5, -18.15) * mm});
            skArc(sketch, "E296", {"start": v(5.5, -18.15) * mm, "mid": v(5.48, -17.9) * mm, "end": v(5.52, -17.63) * mm});
            skLineSegment(sketch, "E297", {"start": v(5.52, -17.63) * mm, "end": v(6.51, -14.58) * mm});
            skLineSegment(sketch, "E298", {"start": v(6.51, -14.58) * mm, "end": v(8.16, -14.58) * mm});
            skArc(sketch, "E299", {"start": v(8.16, -14.58) * mm, "mid": v(8.37, -14.5) * mm, "end": v(8.46, -14.28) * mm});
            skLineSegment(sketch, "E300", {"start": v(8.46, -14.28) * mm, "end": v(8.46, -12.58) * mm});
            skLineSegment(sketch, "E301", {"start": v(8.46, -12.58) * mm, "end": v(7.66, -12.08) * mm});
            skLineSegment(sketch, "E302", {"start": v(7.66, -12.08) * mm, "end": v(-14.44, -12.08) * mm});
            skLineSegment(sketch, "E303", {"start": v(-14.44, -12.08) * mm, "end": v(-15.24, -12.58) * mm});
            skLineSegment(sketch, "E304", {"start": v(-15.24, -12.58) * mm, "end": v(-15.24, -14.28) * mm});
            skArc(sketch, "E305", {"start": v(-15.24, -14.28) * mm, "mid": v(-15.15, -14.5) * mm, "end": v(-14.94, -14.58) * mm});
            skLineSegment(sketch, "E306", {"start": v(-14.94, -14.58) * mm, "end": v(-13.29, -14.58) * mm});
            skLineSegment(sketch, "E307", {"start": v(-13.29, -14.58) * mm, "end": v(-12.3, -17.63) * mm});
            skArc(sketch, "E308", {"start": v(-12.3, -17.63) * mm, "mid": v(-12.25, -17.9) * mm, "end": v(-12.28, -18.15) * mm});
            skArc(sketch, "E309", {"start": v(-12.28, -18.15) * mm, "mid": v(-13.11, -20.2) * mm, "end": v(-14.39, -22) * mm});
            skArc(sketch, "E310", {"start": v(-14.39, -22) * mm, "mid": v(-15.23, -22.43) * mm, "end": v(-16.17, -22.58) * mm});
            skLineSegment(sketch, "E311", {"start": v(-16.17, -22.58) * mm, "end": v(-17.89, -22.58) * mm});
            skLineSegment(sketch, "E312", {"start": v(-17.89, -22.58) * mm, "end": v(-18.39, -23.08) * mm});
            skLineSegment(sketch, "E313", {"start": v(-18.39, -23.08) * mm, "end": v(-18.89, -22.58) * mm});
            skLineSegment(sketch, "E314", {"start": v(-18.89, -22.58) * mm, "end": v(-20.6, -22.58) * mm});
            skArc(sketch, "E315", {"start": v(-20.6, -22.58) * mm, "mid": v(-21.55, -22.43) * mm, "end": v(-22.4, -22) * mm});
            skArc(sketch, "E316", {"start": v(-22.4, -22) * mm, "mid": v(-23.66, -20.2) * mm, "end": v(-24.5, -18.15) * mm});
            skArc(sketch, "E317", {"start": v(-24.5, -18.15) * mm, "mid": v(-24.52, -17.9) * mm, "end": v(-24.48, -17.63) * mm});
            skLineSegment(sketch, "E318", {"start": v(-24.48, -17.63) * mm, "end": v(-23.49, -14.58) * mm});
            skLineSegment(sketch, "E319", {"start": v(-23.49, -14.58) * mm, "end": v(-21.84, -14.58) * mm});
            skArc(sketch, "E320", {"start": v(-21.84, -14.58) * mm, "mid": v(-21.63, -14.5) * mm, "end": v(-21.54, -14.28) * mm});
            skLineSegment(sketch, "E321", {"start": v(-21.54, -14.28) * mm, "end": v(-21.54, -12.58) * mm});
            skLineSegment(sketch, "E322", {"start": v(-21.54, -12.58) * mm, "end": v(-22.34, -12.08) * mm});
            skLineSegment(sketch, "E323", {"start": v(-22.34, -12.08) * mm, "end": v(-32.39, -12.08) * mm});
            skArc(sketch, "E324", {"start": v(-32.39, -12.08) * mm, "mid": v(-33.1, -12.37) * mm, "end": v(-33.39, -13.08) * mm});
            skLineSegment(sketch, "E325", {"start": v(-33.39, -13.08) * mm, "end": v(-33.39, -23.13) * mm});
            skLineSegment(sketch, "E326", {"start": v(-33.39, -23.13) * mm, "end": v(-32.89, -23.93) * mm});
            skLineSegment(sketch, "E327", {"start": v(-32.89, -23.93) * mm, "end": v(-31.19, -23.93) * mm});
            skArc(sketch, "E328", {"start": v(-31.19, -23.93) * mm, "mid": v(-30.98, -23.84) * mm, "end": v(-30.89, -23.63) * mm});
            skLineSegment(sketch, "E329", {"start": v(-30.89, -23.63) * mm, "end": v(-30.89, -21.98) * mm});
            skLineSegment(sketch, "E330", {"start": v(-30.89, -21.98) * mm, "end": v(-27.84, -21) * mm});
            skArc(sketch, "E331", {"start": v(-27.84, -21) * mm, "mid": v(-27.58, -20.95) * mm, "end": v(-27.32, -20.97) * mm});
            skArc(sketch, "E332", {"start": v(-27.32, -20.97) * mm, "mid": v(-25.28, -21.8) * mm, "end": v(-23.48, -23.08) * mm});
            skArc(sketch, "E333", {"start": v(-23.48, -23.08) * mm, "mid": v(-23.04, -23.92) * mm, "end": v(-22.89, -24.86) * mm});
            skLineSegment(sketch, "E334", {"start": v(-22.89, -24.86) * mm, "end": v(-22.89, -26.58) * mm});
            skLineSegment(sketch, "E335", {"start": v(-22.89, -26.58) * mm, "end": v(-22.39, -27.08) * mm});
            skLineSegment(sketch, "E336", {"start": v(-22.39, -27.08) * mm, "end": v(-22.89, -27.58) * mm});
            skLineSegment(sketch, "E337", {"start": v(-22.89, -27.58) * mm, "end": v(-22.89, -29.3) * mm});
            skArc(sketch, "E338", {"start": v(-22.89, -29.3) * mm, "mid": v(-23.04, -30.24) * mm, "end": v(-23.48, -31.08) * mm});
            skArc(sketch, "E339", {"start": v(-23.48, -31.08) * mm, "mid": v(-25.28, -32.36) * mm, "end": v(-27.32, -33.2) * mm});
            skArc(sketch, "E340", {"start": v(-27.32, -33.2) * mm, "mid": v(-27.58, -33.22) * mm, "end": v(-27.84, -33.17) * mm});
            skLineSegment(sketch, "E341", {"start": v(-27.84, -33.17) * mm, "end": v(-30.89, -32.18) * mm});
            skLineSegment(sketch, "E342", {"start": v(-30.89, -32.18) * mm, "end": v(-30.89, -30.53) * mm});
            skArc(sketch, "E343", {"start": v(-30.89, -30.53) * mm, "mid": v(-30.98, -30.32) * mm, "end": v(-31.19, -30.23) * mm});
            skLineSegment(sketch, "E344", {"start": v(-31.19, -30.23) * mm, "end": v(-32.89, -30.23) * mm});
            skLineSegment(sketch, "E345", {"start": v(-32.89, -30.23) * mm, "end": v(-33.39, -31.03) * mm});
            skLineSegment(sketch, "E346", {"start": v(-33.39, -31.03) * mm, "end": v(-33.39, -41.08) * mm});
            skArc(sketch, "E347", {"start": v(-33.39, -41.08) * mm, "mid": v(-33.1, -41.79) * mm, "end": v(-32.39, -42.08) * mm});
            skLineSegment(sketch, "E348", {"start": v(-32.39, -42.08) * mm, "end": v(-22.34, -42.08) * mm});
            skLineSegment(sketch, "E349", {"start": v(-22.34, -42.08) * mm, "end": v(-21.54, -41.58) * mm});
            skLineSegment(sketch, "E350", {"start": v(-21.54, -41.58) * mm, "end": v(-21.54, -39.88) * mm});
            skArc(sketch, "E351", {"start": v(-21.54, -39.88) * mm, "mid": v(-21.63, -39.67) * mm, "end": v(-21.84, -39.58) * mm});
            skLineSegment(sketch, "E352", {"start": v(-21.84, -39.58) * mm, "end": v(-23.49, -39.58) * mm});
            skLineSegment(sketch, "E353", {"start": v(-23.49, -39.58) * mm, "end": v(-24.48, -36.53) * mm});
            skArc(sketch, "E354", {"start": v(-24.48, -36.53) * mm, "mid": v(-24.52, -36.27) * mm, "end": v(-24.5, -36) * mm});
            skArc(sketch, "E355", {"start": v(-24.5, -36) * mm, "mid": v(-23.66, -33.97) * mm, "end": v(-22.4, -32.17) * mm});
            skArc(sketch, "E356", {"start": v(-22.4, -32.17) * mm, "mid": v(-21.55, -31.73) * mm, "end": v(-20.6, -31.58) * mm});
            skLineSegment(sketch, "E357", {"start": v(-20.6, -31.58) * mm, "end": v(-18.89, -31.58) * mm});
            skLineSegment(sketch, "E358", {"start": v(-18.89, -31.58) * mm, "end": v(-18.39, -31.08) * mm});
            skLineSegment(sketch, "E359", {"start": v(-18.39, -31.08) * mm, "end": v(-17.89, -31.58) * mm});
            skLineSegment(sketch, "E360", {"start": v(-17.89, -31.58) * mm, "end": v(-16.17, -31.58) * mm});
            skArc(sketch, "E361", {"start": v(-16.17, -31.58) * mm, "mid": v(-15.23, -31.73) * mm, "end": v(-14.39, -32.17) * mm});
            skArc(sketch, "E362", {"start": v(-14.39, -32.17) * mm, "mid": v(-13.11, -33.97) * mm, "end": v(-12.28, -36) * mm});
            skArc(sketch, "E363", {"start": v(-12.28, -36) * mm, "mid": v(-12.25, -36.27) * mm, "end": v(-12.3, -36.53) * mm});
            skLineSegment(sketch, "E364", {"start": v(-12.3, -36.53) * mm, "end": v(-13.29, -39.58) * mm});
            skLineSegment(sketch, "E365", {"start": v(-13.29, -39.58) * mm, "end": v(-14.94, -39.58) * mm});
            skArc(sketch, "E366", {"start": v(-14.94, -39.58) * mm, "mid": v(-15.15, -39.67) * mm, "end": v(-15.24, -39.88) * mm});
            skLineSegment(sketch, "E367", {"start": v(-15.24, -39.88) * mm, "end": v(-15.24, -41.58) * mm});
            skLineSegment(sketch, "E368", {"start": v(-15.24, -41.58) * mm, "end": v(-14.44, -42.08) * mm});
            skSolve(sketch);
        }
        {
            var Q0;
            Q0=qCreatedBy(makeId("Front.planeOp"),FACE);
            var sketch = newSketch(context, id + "F1", { "sketchPlane" : qUnion([Q0])});
            skLineSegment(sketch, "E369", {"start": v(-2.82, -20.25) * mm, "end": v(-2.82, -15.85) * mm});
            skLineSegment(sketch, "E370", {"start": v(-5.02, -18.05) * mm, "end": v(-0.62, -18.05) * mm});
            skArc(sketch, "E371", {"start": v(-5.5, -19.39) * mm, "mid": v(-5.48, -19.57) * mm, "end": v(-5.56, -19.74) * mm});
            skLineSegment(sketch, "E372", {"start": v(-5.56, -19.74) * mm, "end": v(-6.3, -20.48) * mm});
            skArc(sketch, "E373", {"start": v(-6.3, -20.48) * mm, "mid": v(-6.4, -20.67) * mm, "end": v(-6.32, -20.88) * mm});
            skArc(sketch, "E374", {"start": v(-6.32, -20.88) * mm, "mid": v(-6, -21.24) * mm, "end": v(-5.64, -21.56) * mm});
            skArc(sketch, "E375", {"start": v(-5.64, -21.56) * mm, "mid": v(-5.44, -21.62) * mm, "end": v(-5.24, -21.54) * mm});
            skLineSegment(sketch, "E376", {"start": v(-5.24, -21.54) * mm, "end": v(-4.5, -20.8) * mm});
            skArc(sketch, "E377", {"start": v(-4.5, -20.8) * mm, "mid": v(-4.34, -20.71) * mm, "end": v(-4.16, -20.74) * mm});
            skArc(sketch, "E378", {"start": v(-4.16, -20.74) * mm, "mid": v(-2.82, -21.05) * mm, "end": v(-1.48, -20.74) * mm});
            skArc(sketch, "E379", {"start": v(-1.48, -20.74) * mm, "mid": v(-1.3, -20.71) * mm, "end": v(-1.14, -20.8) * mm});
            skLineSegment(sketch, "E380", {"start": v(-1.14, -20.8) * mm, "end": v(-0.4, -21.54) * mm});
            skArc(sketch, "E381", {"start": v(-0.4, -21.54) * mm, "mid": v(-0.2, -21.62) * mm, "end": v(0, -21.56) * mm});
            skArc(sketch, "E382", {"start": v(0, -21.56) * mm, "mid": v(0.36, -21.24) * mm, "end": v(0.68, -20.88) * mm});
            skArc(sketch, "E383", {"start": v(0.68, -20.88) * mm, "mid": v(0.75, -20.67) * mm, "end": v(0.66, -20.48) * mm});
            skLineSegment(sketch, "E384", {"start": v(0.66, -20.48) * mm, "end": v(-0.08, -19.74) * mm});
            skArc(sketch, "E385", {"start": v(-0.08, -19.74) * mm, "mid": v(-0.16, -19.57) * mm, "end": v(-0.13, -19.39) * mm});
            skArc(sketch, "E386", {"start": v(-0.13, -19.39) * mm, "mid": v(0.18, -18.05) * mm, "end": v(-0.13, -16.72) * mm});
            skArc(sketch, "E387", {"start": v(-0.13, -16.72) * mm, "mid": v(-0.16, -16.54) * mm, "end": v(-0.08, -16.37) * mm});
            skLineSegment(sketch, "E388", {"start": v(-0.08, -16.37) * mm, "end": v(0.66, -15.63) * mm});
            skArc(sketch, "E389", {"start": v(0.66, -15.63) * mm, "mid": v(0.75, -15.44) * mm, "end": v(0.68, -15.23) * mm});
            skArc(sketch, "E390", {"start": v(0.68, -15.23) * mm, "mid": v(0.36, -14.87) * mm, "end": v(0, -14.55) * mm});
            skArc(sketch, "E391", {"start": v(0, -14.55) * mm, "mid": v(-0.2, -14.48) * mm, "end": v(-0.4, -14.57) * mm});
            skLineSegment(sketch, "E392", {"start": v(-0.4, -14.57) * mm, "end": v(-1.14, -15.31) * mm});
            skArc(sketch, "E393", {"start": v(-1.14, -15.31) * mm, "mid": v(-1.3, -15.4) * mm, "end": v(-1.48, -15.37) * mm});
            skArc(sketch, "E394", {"start": v(-1.48, -15.37) * mm, "mid": v(-2.82, -15.05) * mm, "end": v(-4.16, -15.37) * mm});
            skArc(sketch, "E395", {"start": v(-4.16, -15.37) * mm, "mid": v(-4.34, -15.4) * mm, "end": v(-4.5, -15.31) * mm});
            skLineSegment(sketch, "E396", {"start": v(-4.5, -15.31) * mm, "end": v(-5.24, -14.57) * mm});
            skArc(sketch, "E397", {"start": v(-5.24, -14.57) * mm, "mid": v(-5.44, -14.48) * mm, "end": v(-5.64, -14.55) * mm});
            skArc(sketch, "E398", {"start": v(-5.64, -14.55) * mm, "mid": v(-6, -14.87) * mm, "end": v(-6.32, -15.23) * mm});
            skArc(sketch, "E399", {"start": v(-6.32, -15.23) * mm, "mid": v(-6.4, -15.44) * mm, "end": v(-6.3, -15.63) * mm});
            skLineSegment(sketch, "E400", {"start": v(-6.3, -15.63) * mm, "end": v(-5.56, -16.37) * mm});
            skArc(sketch, "E401", {"start": v(-5.56, -16.37) * mm, "mid": v(-5.48, -16.54) * mm, "end": v(-5.5, -16.72) * mm});
            skArc(sketch, "E402", {"start": v(-5.5, -16.72) * mm, "mid": v(-5.82, -18.05) * mm, "end": v(-5.5, -19.39) * mm});
            skLineSegment(sketch, "E403", {"start": v(-5.02, -38.05) * mm, "end": v(-0.62, -38.05) * mm});
            skLineSegment(sketch, "E404", {"start": v(-2.82, -35.85) * mm, "end": v(-2.82, -40.25) * mm});
            skArc(sketch, "E405", {"start": v(-5.5, -36.72) * mm, "mid": v(-5.48, -36.54) * mm, "end": v(-5.56, -36.37) * mm});
            skLineSegment(sketch, "E406", {"start": v(-5.56, -36.37) * mm, "end": v(-6.3, -35.63) * mm});
            skArc(sketch, "E407", {"start": v(-6.3, -35.63) * mm, "mid": v(-6.4, -35.44) * mm, "end": v(-6.33, -35.23) * mm});
            skArc(sketch, "E408", {"start": v(-6.33, -35.23) * mm, "mid": v(-6, -34.87) * mm, "end": v(-5.64, -34.55) * mm});
            skArc(sketch, "E409", {"start": v(-5.64, -34.55) * mm, "mid": v(-5.44, -34.48) * mm, "end": v(-5.24, -34.57) * mm});
            skLineSegment(sketch, "E410", {"start": v(-5.24, -34.57) * mm, "end": v(-4.5, -35.31) * mm});
            skArc(sketch, "E411", {"start": v(-4.5, -35.31) * mm, "mid": v(-4.34, -35.4) * mm, "end": v(-4.16, -35.37) * mm});
            skArc(sketch, "E412", {"start": v(-4.16, -35.37) * mm, "mid": v(-2.82, -35.05) * mm, "end": v(-1.48, -35.37) * mm});
            skArc(sketch, "E413", {"start": v(-1.48, -35.37) * mm, "mid": v(-1.3, -35.4) * mm, "end": v(-1.14, -35.31) * mm});
            skLineSegment(sketch, "E414", {"start": v(-1.14, -35.31) * mm, "end": v(-0.4, -34.57) * mm});
            skArc(sketch, "E415", {"start": v(-0.4, -34.57) * mm, "mid": v(-0.2, -34.48) * mm, "end": v(0, -34.55) * mm});
            skArc(sketch, "E416", {"start": v(0, -34.55) * mm, "mid": v(0.36, -34.87) * mm, "end": v(0.68, -35.23) * mm});
            skArc(sketch, "E417", {"start": v(0.68, -35.23) * mm, "mid": v(0.75, -35.44) * mm, "end": v(0.66, -35.63) * mm});
            skLineSegment(sketch, "E418", {"start": v(0.66, -35.63) * mm, "end": v(-0.08, -36.37) * mm});
            skArc(sketch, "E419", {"start": v(-0.08, -36.37) * mm, "mid": v(-0.16, -36.54) * mm, "end": v(-0.13, -36.72) * mm});
            skArc(sketch, "E420", {"start": v(-0.13, -36.72) * mm, "mid": v(0.18, -38.05) * mm, "end": v(-0.14, -39.4) * mm});
            skArc(sketch, "E421", {"start": v(-0.14, -39.4) * mm, "mid": v(-0.16, -39.57) * mm, "end": v(-0.08, -39.74) * mm});
            skLineSegment(sketch, "E422", {"start": v(-0.08, -39.74) * mm, "end": v(0.66, -40.48) * mm});
            skArc(sketch, "E423", {"start": v(0.66, -40.48) * mm, "mid": v(0.75, -40.67) * mm, "end": v(0.68, -40.88) * mm});
            skArc(sketch, "E424", {"start": v(0.68, -40.88) * mm, "mid": v(0.36, -41.24) * mm, "end": v(0, -41.56) * mm});
            skArc(sketch, "E425", {"start": v(0, -41.56) * mm, "mid": v(-0.2, -41.63) * mm, "end": v(-0.4, -41.54) * mm});
            skLineSegment(sketch, "E426", {"start": v(-0.4, -41.54) * mm, "end": v(-1.14, -40.8) * mm});
            skArc(sketch, "E427", {"start": v(-1.14, -40.8) * mm, "mid": v(-1.3, -40.71) * mm, "end": v(-1.49, -40.74) * mm});
            skArc(sketch, "E428", {"start": v(-1.49, -40.74) * mm, "mid": v(-2.82, -41.05) * mm, "end": v(-4.16, -40.74) * mm});
            skArc(sketch, "E429", {"start": v(-4.16, -40.74) * mm, "mid": v(-4.34, -40.71) * mm, "end": v(-4.5, -40.8) * mm});
            skLineSegment(sketch, "E430", {"start": v(-4.5, -40.8) * mm, "end": v(-5.24, -41.54) * mm});
            skArc(sketch, "E431", {"start": v(-5.24, -41.54) * mm, "mid": v(-5.44, -41.62) * mm, "end": v(-5.64, -41.56) * mm});
            skArc(sketch, "E432", {"start": v(-5.64, -41.56) * mm, "mid": v(-6, -41.24) * mm, "end": v(-6.33, -40.88) * mm});
            skArc(sketch, "E433", {"start": v(-6.33, -40.88) * mm, "mid": v(-6.4, -40.67) * mm, "end": v(-6.3, -40.48) * mm});
            skLineSegment(sketch, "E434", {"start": v(-6.3, -40.48) * mm, "end": v(-5.56, -39.74) * mm});
            skArc(sketch, "E435", {"start": v(-5.56, -39.74) * mm, "mid": v(-5.48, -39.57) * mm, "end": v(-5.5, -39.4) * mm});
            skArc(sketch, "E436", {"start": v(-5.5, -39.4) * mm, "mid": v(-5.82, -38.05) * mm, "end": v(-5.5, -36.72) * mm});
            skArc(sketch, "E437", {"start": v(-20.13, -36.72) * mm, "mid": v(-20.16, -36.54) * mm, "end": v(-20.07, -36.37) * mm});
            skLineSegment(sketch, "E438", {"start": v(-20.07, -36.37) * mm, "end": v(-19.33, -35.63) * mm});
            skArc(sketch, "E439", {"start": v(-19.33, -35.63) * mm, "mid": v(-19.25, -35.44) * mm, "end": v(-19.31, -35.23) * mm});
            skArc(sketch, "E440", {"start": v(-19.31, -35.23) * mm, "mid": v(-19.64, -34.87) * mm, "end": v(-20, -34.55) * mm});
            skArc(sketch, "E441", {"start": v(-20, -34.55) * mm, "mid": v(-20.2, -34.48) * mm, "end": v(-20.4, -34.57) * mm});
            skLineSegment(sketch, "E442", {"start": v(-20.4, -34.57) * mm, "end": v(-21.14, -35.31) * mm});
            skArc(sketch, "E443", {"start": v(-21.14, -35.31) * mm, "mid": v(-21.3, -35.4) * mm, "end": v(-21.48, -35.37) * mm});
            skArc(sketch, "E444", {"start": v(-21.48, -35.37) * mm, "mid": v(-22.82, -35.05) * mm, "end": v(-24.15, -35.37) * mm});
            skArc(sketch, "E445", {"start": v(-24.15, -35.37) * mm, "mid": v(-24.34, -35.4) * mm, "end": v(-24.5, -35.31) * mm});
            skLineSegment(sketch, "E446", {"start": v(-24.5, -35.31) * mm, "end": v(-25.24, -34.57) * mm});
            skArc(sketch, "E447", {"start": v(-25.24, -34.57) * mm, "mid": v(-25.44, -34.48) * mm, "end": v(-25.64, -34.55) * mm});
            skArc(sketch, "E448", {"start": v(-25.64, -34.55) * mm, "mid": v(-26, -34.87) * mm, "end": v(-26.32, -35.23) * mm});
            skArc(sketch, "E449", {"start": v(-26.32, -35.23) * mm, "mid": v(-26.39, -35.44) * mm, "end": v(-26.3, -35.63) * mm});
            skLineSegment(sketch, "E450", {"start": v(-26.3, -35.63) * mm, "end": v(-25.56, -36.37) * mm});
            skArc(sketch, "E451", {"start": v(-25.56, -36.37) * mm, "mid": v(-25.48, -36.54) * mm, "end": v(-25.5, -36.72) * mm});
            skArc(sketch, "E452", {"start": v(-25.5, -36.72) * mm, "mid": v(-25.82, -38.05) * mm, "end": v(-25.5, -39.4) * mm});
            skArc(sketch, "E453", {"start": v(-25.5, -39.4) * mm, "mid": v(-25.48, -39.57) * mm, "end": v(-25.56, -39.74) * mm});
            skLineSegment(sketch, "E454", {"start": v(-25.56, -39.74) * mm, "end": v(-26.3, -40.48) * mm});
            skArc(sketch, "E455", {"start": v(-26.3, -40.48) * mm, "mid": v(-26.39, -40.67) * mm, "end": v(-26.32, -40.88) * mm});
            skArc(sketch, "E456", {"start": v(-26.32, -40.88) * mm, "mid": v(-26, -41.24) * mm, "end": v(-25.64, -41.56) * mm});
            skArc(sketch, "E457", {"start": v(-25.64, -41.56) * mm, "mid": v(-25.44, -41.63) * mm, "end": v(-25.24, -41.54) * mm});
            skLineSegment(sketch, "E458", {"start": v(-25.24, -41.54) * mm, "end": v(-24.5, -40.8) * mm});
            skArc(sketch, "E459", {"start": v(-24.5, -40.8) * mm, "mid": v(-24.33, -40.71) * mm, "end": v(-24.15, -40.74) * mm});
            skArc(sketch, "E460", {"start": v(-24.15, -40.74) * mm, "mid": v(-22.82, -41.05) * mm, "end": v(-21.48, -40.74) * mm});
            skArc(sketch, "E461", {"start": v(-21.48, -40.74) * mm, "mid": v(-21.3, -40.71) * mm, "end": v(-21.14, -40.8) * mm});
            skLineSegment(sketch, "E462", {"start": v(-21.14, -40.8) * mm, "end": v(-20.4, -41.54) * mm});
            skArc(sketch, "E463", {"start": v(-20.4, -41.54) * mm, "mid": v(-20.2, -41.62) * mm, "end": v(-20, -41.56) * mm});
            skArc(sketch, "E464", {"start": v(-20, -41.56) * mm, "mid": v(-19.63, -41.24) * mm, "end": v(-19.31, -40.88) * mm});
            skArc(sketch, "E465", {"start": v(-19.31, -40.88) * mm, "mid": v(-19.25, -40.67) * mm, "end": v(-19.33, -40.48) * mm});
            skLineSegment(sketch, "E466", {"start": v(-19.33, -40.48) * mm, "end": v(-20.07, -39.74) * mm});
            skArc(sketch, "E467", {"start": v(-20.07, -39.74) * mm, "mid": v(-20.16, -39.57) * mm, "end": v(-20.13, -39.4) * mm});
            skArc(sketch, "E468", {"start": v(-20.13, -39.4) * mm, "mid": v(-19.82, -38.05) * mm, "end": v(-20.13, -36.72) * mm});
            skLineSegment(sketch, "E469", {"start": v(-22.82, -35.85) * mm, "end": v(-22.82, -40.25) * mm});
            skLineSegment(sketch, "E470", {"start": v(-20.62, -38.05) * mm, "end": v(-25.02, -38.05) * mm});
            skLineSegment(sketch, "E471", {"start": v(-20.62, -18.05) * mm, "end": v(-25.02, -18.05) * mm});
            skLineSegment(sketch, "E472", {"start": v(-22.82, -20.25) * mm, "end": v(-22.82, -15.85) * mm});
            skLineSegment(sketch, "E473", {"start": v(2.64, -28.05) * mm, "end": v(-29.04, -28.05) * mm});
            skLineSegment(sketch, "E474", {"start": v(-12.82, -44) * mm, "end": v(-12.82, -12.06) * mm});
            skArc(sketch, "E475", {"start": v(-9.58, -26.47) * mm, "mid": v(-9.36, -26.3) * mm, "end": v(-9.38, -26.02) * mm});
            skArc(sketch, "E476", {"start": v(-9.38, -26.02) * mm, "mid": v(-10, -25.23) * mm, "end": v(-10.78, -24.61) * mm});
            skArc(sketch, "E477", {"start": v(-10.78, -24.61) * mm, "mid": v(-11.06, -24.6) * mm, "end": v(-11.23, -24.82) * mm});
            skLineSegment(sketch, "E478", {"start": v(-11.23, -24.82) * mm, "end": v(-11.37, -25.56) * mm});
            skArc(sketch, "E479", {"start": v(-11.37, -25.56) * mm, "mid": v(-11.52, -25.77) * mm, "end": v(-11.78, -25.78) * mm});
            skArc(sketch, "E480", {"start": v(-11.78, -25.78) * mm, "mid": v(-12.82, -25.55) * mm, "end": v(-13.85, -25.78) * mm});
            skArc(sketch, "E481", {"start": v(-13.85, -25.78) * mm, "mid": v(-14.11, -25.77) * mm, "end": v(-14.27, -25.56) * mm});
            skLineSegment(sketch, "E482", {"start": v(-14.27, -25.56) * mm, "end": v(-14.4, -24.82) * mm});
            skArc(sketch, "E483", {"start": v(-14.4, -24.82) * mm, "mid": v(-14.57, -24.6) * mm, "end": v(-14.85, -24.61) * mm});
            skArc(sketch, "E484", {"start": v(-14.85, -24.61) * mm, "mid": v(-15.65, -25.23) * mm, "end": v(-16.26, -26.02) * mm});
            skArc(sketch, "E485", {"start": v(-16.26, -26.02) * mm, "mid": v(-16.27, -26.3) * mm, "end": v(-16.06, -26.47) * mm});
            skLineSegment(sketch, "E486", {"start": v(-16.06, -26.47) * mm, "end": v(-15.31, -26.6) * mm});
            skArc(sketch, "E487", {"start": v(-15.31, -26.6) * mm, "mid": v(-15.1, -26.76) * mm, "end": v(-15.1, -27.02) * mm});
            skArc(sketch, "E488", {"start": v(-15.1, -27.02) * mm, "mid": v(-15.32, -28.05) * mm, "end": v(-15.1, -29.09) * mm});
            skArc(sketch, "E489", {"start": v(-15.1, -29.09) * mm, "mid": v(-15.1, -29.35) * mm, "end": v(-15.31, -29.5) * mm});
            skLineSegment(sketch, "E490", {"start": v(-15.31, -29.5) * mm, "end": v(-16.06, -29.64) * mm});
            skArc(sketch, "E491", {"start": v(-16.06, -29.64) * mm, "mid": v(-16.27, -29.81) * mm, "end": v(-16.26, -30.09) * mm});
            skArc(sketch, "E492", {"start": v(-16.26, -30.09) * mm, "mid": v(-15.65, -30.88) * mm, "end": v(-14.85, -31.5) * mm});
            skArc(sketch, "E493", {"start": v(-14.85, -31.5) * mm, "mid": v(-14.57, -31.51) * mm, "end": v(-14.4, -31.3) * mm});
            skLineSegment(sketch, "E494", {"start": v(-14.4, -31.3) * mm, "end": v(-14.27, -30.55) * mm});
            skArc(sketch, "E495", {"start": v(-14.27, -30.55) * mm, "mid": v(-14.11, -30.34) * mm, "end": v(-13.85, -30.33) * mm});
            skArc(sketch, "E496", {"start": v(-13.85, -30.33) * mm, "mid": v(-12.82, -30.55) * mm, "end": v(-11.78, -30.33) * mm});
            skArc(sketch, "E497", {"start": v(-11.78, -30.33) * mm, "mid": v(-11.52, -30.34) * mm, "end": v(-11.37, -30.55) * mm});
            skLineSegment(sketch, "E498", {"start": v(-11.37, -30.55) * mm, "end": v(-11.23, -31.3) * mm});
            skArc(sketch, "E499", {"start": v(-11.23, -31.3) * mm, "mid": v(-11.06, -31.51) * mm, "end": v(-10.78, -31.5) * mm});
            skArc(sketch, "E500", {"start": v(-10.78, -31.5) * mm, "mid": v(-10, -30.88) * mm, "end": v(-9.38, -30.09) * mm});
            skArc(sketch, "E501", {"start": v(-9.38, -30.09) * mm, "mid": v(-9.36, -29.81) * mm, "end": v(-9.58, -29.64) * mm});
            skLineSegment(sketch, "E502", {"start": v(-9.58, -29.64) * mm, "end": v(-10.32, -29.5) * mm});
            skArc(sketch, "E503", {"start": v(-10.32, -29.5) * mm, "mid": v(-10.53, -29.35) * mm, "end": v(-10.54, -29.09) * mm});
            skArc(sketch, "E504", {"start": v(-10.54, -29.09) * mm, "mid": v(-10.32, -28.05) * mm, "end": v(-10.54, -27.02) * mm});
            skArc(sketch, "E505", {"start": v(-10.54, -27.02) * mm, "mid": v(-10.53, -26.76) * mm, "end": v(-10.32, -26.6) * mm});
            skLineSegment(sketch, "E506", {"start": v(-10.32, -26.6) * mm, "end": v(-9.58, -26.47) * mm});
            skArc(sketch, "E507", {"start": v(-20.13, -19.39) * mm, "mid": v(-20.16, -19.57) * mm, "end": v(-20.08, -19.74) * mm});
            skLineSegment(sketch, "E508", {"start": v(-20.08, -19.74) * mm, "end": v(-19.33, -20.48) * mm});
            skArc(sketch, "E509", {"start": v(-19.33, -20.48) * mm, "mid": v(-19.25, -20.67) * mm, "end": v(-19.31, -20.88) * mm});
            skArc(sketch, "E510", {"start": v(-19.31, -20.88) * mm, "mid": v(-19.64, -21.24) * mm, "end": v(-20, -21.56) * mm});
            skArc(sketch, "E511", {"start": v(-20, -21.56) * mm, "mid": v(-20.2, -21.62) * mm, "end": v(-20.4, -21.54) * mm});
            skLineSegment(sketch, "E512", {"start": v(-20.4, -21.54) * mm, "end": v(-21.14, -20.8) * mm});
            skArc(sketch, "E513", {"start": v(-21.14, -20.8) * mm, "mid": v(-21.3, -20.71) * mm, "end": v(-21.48, -20.74) * mm});
            skArc(sketch, "E514", {"start": v(-21.48, -20.74) * mm, "mid": v(-22.82, -21.05) * mm, "end": v(-24.15, -20.74) * mm});
            skArc(sketch, "E515", {"start": v(-24.15, -20.74) * mm, "mid": v(-24.34, -20.71) * mm, "end": v(-24.5, -20.8) * mm});
            skLineSegment(sketch, "E516", {"start": v(-24.5, -20.8) * mm, "end": v(-25.24, -21.54) * mm});
            skArc(sketch, "E517", {"start": v(-25.24, -21.54) * mm, "mid": v(-25.44, -21.62) * mm, "end": v(-25.64, -21.56) * mm});
            skArc(sketch, "E518", {"start": v(-25.64, -21.56) * mm, "mid": v(-26, -21.24) * mm, "end": v(-26.32, -20.88) * mm});
            skArc(sketch, "E519", {"start": v(-26.32, -20.88) * mm, "mid": v(-26.39, -20.67) * mm, "end": v(-26.3, -20.48) * mm});
            skLineSegment(sketch, "E520", {"start": v(-26.3, -20.48) * mm, "end": v(-25.56, -19.74) * mm});
            skArc(sketch, "E521", {"start": v(-25.56, -19.74) * mm, "mid": v(-25.48, -19.57) * mm, "end": v(-25.5, -19.39) * mm});
            skArc(sketch, "E522", {"start": v(-25.5, -19.39) * mm, "mid": v(-25.82, -18.05) * mm, "end": v(-25.5, -16.72) * mm});
            skArc(sketch, "E523", {"start": v(-25.5, -16.72) * mm, "mid": v(-25.48, -16.54) * mm, "end": v(-25.56, -16.37) * mm});
            skLineSegment(sketch, "E524", {"start": v(-25.56, -16.37) * mm, "end": v(-26.3, -15.63) * mm});
            skArc(sketch, "E525", {"start": v(-26.3, -15.63) * mm, "mid": v(-26.39, -15.44) * mm, "end": v(-26.32, -15.23) * mm});
            skArc(sketch, "E526", {"start": v(-26.32, -15.23) * mm, "mid": v(-26, -14.87) * mm, "end": v(-25.64, -14.55) * mm});
            skArc(sketch, "E527", {"start": v(-25.64, -14.55) * mm, "mid": v(-25.44, -14.48) * mm, "end": v(-25.24, -14.57) * mm});
            skLineSegment(sketch, "E528", {"start": v(-25.24, -14.57) * mm, "end": v(-24.5, -15.31) * mm});
            skArc(sketch, "E529", {"start": v(-24.5, -15.31) * mm, "mid": v(-24.34, -15.4) * mm, "end": v(-24.15, -15.37) * mm});
            skArc(sketch, "E530", {"start": v(-24.15, -15.37) * mm, "mid": v(-22.82, -15.05) * mm, "end": v(-21.48, -15.37) * mm});
            skArc(sketch, "E531", {"start": v(-21.48, -15.37) * mm, "mid": v(-21.3, -15.4) * mm, "end": v(-21.14, -15.31) * mm});
            skLineSegment(sketch, "E532", {"start": v(-21.14, -15.31) * mm, "end": v(-20.4, -14.57) * mm});
            skArc(sketch, "E533", {"start": v(-20.4, -14.57) * mm, "mid": v(-20.2, -14.48) * mm, "end": v(-20, -14.55) * mm});
            skArc(sketch, "E534", {"start": v(-20, -14.55) * mm, "mid": v(-19.64, -14.87) * mm, "end": v(-19.31, -15.23) * mm});
            skArc(sketch, "E535", {"start": v(-19.31, -15.23) * mm, "mid": v(-19.25, -15.44) * mm, "end": v(-19.33, -15.63) * mm});
            skLineSegment(sketch, "E536", {"start": v(-19.33, -15.63) * mm, "end": v(-20.08, -16.37) * mm});
            skArc(sketch, "E537", {"start": v(-20.08, -16.37) * mm, "mid": v(-20.16, -16.54) * mm, "end": v(-20.13, -16.72) * mm});
            skArc(sketch, "E538", {"start": v(-20.13, -16.72) * mm, "mid": v(-19.82, -18.05) * mm, "end": v(-20.13, -19.39) * mm});
            skLineSegment(sketch, "E539", {"start": v(-8.87, -43.05) * mm, "end": v(-9.67, -42.55) * mm});
            skLineSegment(sketch, "E540", {"start": v(-9.67, -42.55) * mm, "end": v(-9.67, -40.85) * mm});
            skArc(sketch, "E541", {"start": v(-9.67, -40.85) * mm, "mid": v(-9.58, -40.64) * mm, "end": v(-9.37, -40.55) * mm});
            skLineSegment(sketch, "E542", {"start": v(-9.37, -40.55) * mm, "end": v(-7.72, -40.55) * mm});
            skLineSegment(sketch, "E543", {"start": v(-7.72, -40.55) * mm, "end": v(-6.73, -37.5) * mm});
            skArc(sketch, "E544", {"start": v(-6.73, -37.5) * mm, "mid": v(-6.68, -37.24) * mm, "end": v(-6.7, -36.98) * mm});
            skArc(sketch, "E545", {"start": v(-6.7, -36.98) * mm, "mid": v(-7.54, -34.94) * mm, "end": v(-8.81, -33.14) * mm});
            skArc(sketch, "E546", {"start": v(-8.81, -33.14) * mm, "mid": v(-9.66, -32.7) * mm, "end": v(-10.6, -32.55) * mm});
            skLineSegment(sketch, "E547", {"start": v(-10.6, -32.55) * mm, "end": v(-12.32, -32.55) * mm});
            skLineSegment(sketch, "E548", {"start": v(-12.32, -32.55) * mm, "end": v(-12.82, -32.05) * mm});
            skLineSegment(sketch, "E549", {"start": v(-12.82, -32.05) * mm, "end": v(-13.32, -32.55) * mm});
            skLineSegment(sketch, "E550", {"start": v(-13.32, -32.55) * mm, "end": v(-15.04, -32.55) * mm});
            skArc(sketch, "E551", {"start": v(-15.04, -32.55) * mm, "mid": v(-15.98, -32.7) * mm, "end": v(-16.82, -33.14) * mm});
            skArc(sketch, "E552", {"start": v(-16.82, -33.14) * mm, "mid": v(-18.1, -34.94) * mm, "end": v(-18.93, -36.98) * mm});
            skArc(sketch, "E553", {"start": v(-18.93, -36.98) * mm, "mid": v(-18.95, -37.24) * mm, "end": v(-18.9, -37.5) * mm});
            skLineSegment(sketch, "E554", {"start": v(-18.9, -37.5) * mm, "end": v(-17.92, -40.55) * mm});
            skLineSegment(sketch, "E555", {"start": v(-17.92, -40.55) * mm, "end": v(-16.27, -40.55) * mm});
            skArc(sketch, "E556", {"start": v(-16.27, -40.55) * mm, "mid": v(-16.06, -40.64) * mm, "end": v(-15.97, -40.85) * mm});
            skLineSegment(sketch, "E557", {"start": v(-15.97, -40.85) * mm, "end": v(-15.97, -42.55) * mm});
            skLineSegment(sketch, "E558", {"start": v(-15.97, -42.55) * mm, "end": v(-16.77, -43.05) * mm});
            skLineSegment(sketch, "E559", {"start": v(-16.77, -43.05) * mm, "end": v(-26.82, -43.05) * mm});
            skArc(sketch, "E560", {"start": v(-26.82, -43.05) * mm, "mid": v(-27.52, -42.76) * mm, "end": v(-27.82, -42.05) * mm});
            skLineSegment(sketch, "E561", {"start": v(-27.82, -42.05) * mm, "end": v(-27.82, -32) * mm});
            skLineSegment(sketch, "E562", {"start": v(-27.82, -32) * mm, "end": v(-27.32, -31.2) * mm});
            skLineSegment(sketch, "E563", {"start": v(-27.32, -31.2) * mm, "end": v(-25.62, -31.2) * mm});
            skArc(sketch, "E564", {"start": v(-25.62, -31.2) * mm, "mid": v(-25.4, -31.3) * mm, "end": v(-25.32, -31.5) * mm});
            skLineSegment(sketch, "E565", {"start": v(-25.32, -31.5) * mm, "end": v(-25.32, -33.15) * mm});
            skLineSegment(sketch, "E566", {"start": v(-25.32, -33.15) * mm, "end": v(-22.27, -34.14) * mm});
            skArc(sketch, "E567", {"start": v(-22.27, -34.14) * mm, "mid": v(-22, -34.19) * mm, "end": v(-21.75, -34.17) * mm});
            skArc(sketch, "E568", {"start": v(-21.75, -34.17) * mm, "mid": v(-19.7, -33.33) * mm, "end": v(-17.9, -32.06) * mm});
            skArc(sketch, "E569", {"start": v(-17.9, -32.06) * mm, "mid": v(-17.47, -31.21) * mm, "end": v(-17.32, -30.27) * mm});
            skLineSegment(sketch, "E570", {"start": v(-17.32, -30.27) * mm, "end": v(-17.32, -28.55) * mm});
            skLineSegment(sketch, "E571", {"start": v(-17.32, -28.55) * mm, "end": v(-16.82, -28.05) * mm});
            skLineSegment(sketch, "E572", {"start": v(-16.82, -28.05) * mm, "end": v(-17.32, -27.55) * mm});
            skLineSegment(sketch, "E573", {"start": v(-17.32, -27.55) * mm, "end": v(-17.32, -25.84) * mm});
            skArc(sketch, "E574", {"start": v(-17.32, -25.84) * mm, "mid": v(-17.47, -24.9) * mm, "end": v(-17.9, -24.05) * mm});
            skArc(sketch, "E575", {"start": v(-17.9, -24.05) * mm, "mid": v(-19.7, -22.78) * mm, "end": v(-21.75, -21.94) * mm});
            skArc(sketch, "E576", {"start": v(-21.75, -21.94) * mm, "mid": v(-22, -21.92) * mm, "end": v(-22.27, -21.97) * mm});
            skLineSegment(sketch, "E577", {"start": v(-22.27, -21.97) * mm, "end": v(-25.32, -22.95) * mm});
            skLineSegment(sketch, "E578", {"start": v(-25.32, -22.95) * mm, "end": v(-25.32, -24.6) * mm});
            skArc(sketch, "E579", {"start": v(-25.32, -24.6) * mm, "mid": v(-25.4, -24.82) * mm, "end": v(-25.62, -24.9) * mm});
            skLineSegment(sketch, "E580", {"start": v(-25.62, -24.9) * mm, "end": v(-27.32, -24.9) * mm});
            skLineSegment(sketch, "E581", {"start": v(-27.32, -24.9) * mm, "end": v(-27.82, -24.1) * mm});
            skLineSegment(sketch, "E582", {"start": v(-27.82, -24.1) * mm, "end": v(-27.82, -14.05) * mm});
            skArc(sketch, "E583", {"start": v(-27.82, -14.05) * mm, "mid": v(-27.52, -13.35) * mm, "end": v(-26.82, -13.05) * mm});
            skLineSegment(sketch, "E584", {"start": v(-26.82, -13.05) * mm, "end": v(-16.77, -13.05) * mm});
            skLineSegment(sketch, "E585", {"start": v(-16.77, -13.05) * mm, "end": v(-15.97, -13.55) * mm});
            skLineSegment(sketch, "E586", {"start": v(-15.97, -13.55) * mm, "end": v(-15.97, -15.25) * mm});
            skArc(sketch, "E587", {"start": v(-15.97, -15.25) * mm, "mid": v(-16.06, -15.47) * mm, "end": v(-16.27, -15.55) * mm});
            skLineSegment(sketch, "E588", {"start": v(-16.27, -15.55) * mm, "end": v(-17.92, -15.55) * mm});
            skLineSegment(sketch, "E589", {"start": v(-17.92, -15.55) * mm, "end": v(-18.9, -18.6) * mm});
            skArc(sketch, "E590", {"start": v(-18.9, -18.6) * mm, "mid": v(-18.95, -18.86) * mm, "end": v(-18.93, -19.13) * mm});
            skArc(sketch, "E591", {"start": v(-18.93, -19.13) * mm, "mid": v(-18.1, -21.16) * mm, "end": v(-16.82, -22.96) * mm});
            skArc(sketch, "E592", {"start": v(-16.82, -22.96) * mm, "mid": v(-15.98, -23.4) * mm, "end": v(-15.04, -23.55) * mm});
            skLineSegment(sketch, "E593", {"start": v(-15.04, -23.55) * mm, "end": v(-13.32, -23.55) * mm});
            skLineSegment(sketch, "E594", {"start": v(-13.32, -23.55) * mm, "end": v(-12.82, -24.05) * mm});
            skLineSegment(sketch, "E595", {"start": v(-12.82, -24.05) * mm, "end": v(-12.32, -23.55) * mm});
            skLineSegment(sketch, "E596", {"start": v(-12.32, -23.55) * mm, "end": v(-10.6, -23.55) * mm});
            skArc(sketch, "E597", {"start": v(-10.6, -23.55) * mm, "mid": v(-9.66, -23.4) * mm, "end": v(-8.81, -22.96) * mm});
            skArc(sketch, "E598", {"start": v(-8.81, -22.96) * mm, "mid": v(-7.54, -21.16) * mm, "end": v(-6.7, -19.13) * mm});
            skArc(sketch, "E599", {"start": v(-6.7, -19.13) * mm, "mid": v(-6.68, -18.86) * mm, "end": v(-6.73, -18.6) * mm});
            skLineSegment(sketch, "E600", {"start": v(-6.73, -18.6) * mm, "end": v(-7.72, -15.55) * mm});
            skLineSegment(sketch, "E601", {"start": v(-7.72, -15.55) * mm, "end": v(-9.37, -15.55) * mm});
            skArc(sketch, "E602", {"start": v(-9.37, -15.55) * mm, "mid": v(-9.58, -15.47) * mm, "end": v(-9.67, -15.25) * mm});
            skLineSegment(sketch, "E603", {"start": v(-9.67, -15.25) * mm, "end": v(-9.67, -13.55) * mm});
            skLineSegment(sketch, "E604", {"start": v(-9.67, -13.55) * mm, "end": v(-8.87, -13.05) * mm});
            skLineSegment(sketch, "E605", {"start": v(-8.87, -13.05) * mm, "end": v(1.18, -13.05) * mm});
            skArc(sketch, "E606", {"start": v(1.18, -13.05) * mm, "mid": v(1.89, -13.35) * mm, "end": v(2.18, -14.05) * mm});
            skLineSegment(sketch, "E607", {"start": v(2.18, -14.05) * mm, "end": v(2.18, -24.1) * mm});
            skLineSegment(sketch, "E608", {"start": v(2.18, -24.1) * mm, "end": v(1.68, -24.9) * mm});
            skLineSegment(sketch, "E609", {"start": v(1.68, -24.9) * mm, "end": v(-0.02, -24.9) * mm});
            skArc(sketch, "E610", {"start": v(-0.02, -24.9) * mm, "mid": v(-0.23, -24.82) * mm, "end": v(-0.32, -24.6) * mm});
            skLineSegment(sketch, "E611", {"start": v(-0.32, -24.6) * mm, "end": v(-0.32, -22.95) * mm});
            skLineSegment(sketch, "E612", {"start": v(-0.32, -22.95) * mm, "end": v(-3.37, -21.97) * mm});
            skArc(sketch, "E613", {"start": v(-3.37, -21.97) * mm, "mid": v(-3.63, -21.92) * mm, "end": v(-3.9, -21.94) * mm});
            skArc(sketch, "E614", {"start": v(-3.9, -21.94) * mm, "mid": v(-5.93, -22.78) * mm, "end": v(-7.73, -24.05) * mm});
            skArc(sketch, "E615", {"start": v(-7.73, -24.05) * mm, "mid": v(-8.17, -24.9) * mm, "end": v(-8.32, -25.84) * mm});
            skLineSegment(sketch, "E616", {"start": v(-8.32, -25.84) * mm, "end": v(-8.32, -27.55) * mm});
            skLineSegment(sketch, "E617", {"start": v(-8.32, -27.55) * mm, "end": v(-8.82, -28.05) * mm});
            skLineSegment(sketch, "E618", {"start": v(-8.82, -28.05) * mm, "end": v(-8.32, -28.55) * mm});
            skLineSegment(sketch, "E619", {"start": v(-8.32, -28.55) * mm, "end": v(-8.32, -30.27) * mm});
            skArc(sketch, "E620", {"start": v(-8.32, -30.27) * mm, "mid": v(-8.17, -31.21) * mm, "end": v(-7.73, -32.06) * mm});
            skArc(sketch, "E621", {"start": v(-7.73, -32.06) * mm, "mid": v(-5.93, -33.33) * mm, "end": v(-3.9, -34.17) * mm});
            skArc(sketch, "E622", {"start": v(-3.9, -34.17) * mm, "mid": v(-3.63, -34.19) * mm, "end": v(-3.37, -34.14) * mm});
            skLineSegment(sketch, "E623", {"start": v(-3.37, -34.14) * mm, "end": v(-0.32, -33.15) * mm});
            skLineSegment(sketch, "E624", {"start": v(-0.32, -33.15) * mm, "end": v(-0.32, -31.5) * mm});
            skArc(sketch, "E625", {"start": v(-0.32, -31.5) * mm, "mid": v(-0.23, -31.3) * mm, "end": v(-0.02, -31.2) * mm});
            skLineSegment(sketch, "E626", {"start": v(-0.02, -31.2) * mm, "end": v(1.68, -31.2) * mm});
            skLineSegment(sketch, "E627", {"start": v(1.68, -31.2) * mm, "end": v(2.18, -32) * mm});
            skLineSegment(sketch, "E628", {"start": v(2.18, -32) * mm, "end": v(2.18, -42.05) * mm});
            skArc(sketch, "E629", {"start": v(2.18, -42.05) * mm, "mid": v(1.89, -42.76) * mm, "end": v(1.18, -43.05) * mm});
            skLineSegment(sketch, "E630", {"start": v(1.18, -43.05) * mm, "end": v(-8.87, -43.05) * mm});
            skSolve(sketch);
        }
        {
            var Q0;
            {var subQ1=sQuery(id+"F1.wireOp",EDGE,"E481");Q0=makeQuery(id+"F1.imprint","IMPRINT",FACE,{"disambiguationData":[TD([[makeQuery(id+"F1.imprint","IMPRINT",EDGE,{"derivedFrom":subQ1}),-1.0]])]});}
            var Q1;
            Q1=makeQuery(id+"F1.imprint","IMPRINT",FACE,{"disambiguationData":[TD([[makeQuery(id+"F1.imprint","IMPRINT",EDGE,{"derivedFrom":sQuery(id+"F1.wireOp",EDGE,"E371")}),-1.0]])]});
            var Q2;
            Q2=makeQuery(id+"F1.imprint","IMPRINT",FACE,{"disambiguationData":[TD([[makeQuery(id+"F1.imprint","IMPRINT",EDGE,{"derivedFrom":sQuery(id+"F1.wireOp",EDGE,"E405")}),1.0]])]});
            var Q3;
            Q3=makeQuery(id+"F1.imprint","IMPRINT",FACE,{"disambiguationData":[TD([[makeQuery(id+"F1.imprint","IMPRINT",EDGE,{"derivedFrom":sQuery(id+"F1.wireOp",EDGE,"E437")}),-1.0]])]});
            extrude(context, id + "F2", {"entities" : qUnion([Q0, Q1, Q2, Q3]), "depth" : 500 * mm, "offsetDistance" : 25 * mm});
        }
        {
            var Q0;
            Q0=makeQuery(id+"F0.imprint","IMPRINT",FACE,{"disambiguationData":[TD([[makeQuery(id+"F0.imprint","IMPRINT",EDGE,{"derivedFrom":sQuery(id+"F0.wireOp",EDGE,"E103")}),-1.0]])]});
            var Q1;
            {var subQ6=sQuery(id+"F0.wireOp",EDGE,"E125");Q1=makeQuery(id+"F0.imprint","IMPRINT",FACE,{"disambiguationData":[TD([[makeQuery(id+"F0.imprint","IMPRINT",EDGE,{"derivedFrom":subQ6}),-1.0]])]});}
            var Q2;
            {var subQ11=sQuery(id+"F0.wireOp",EDGE,"E60");Q2=makeQuery(id+"F0.imprint","IMPRINT",FACE,{"disambiguationData":[TD([[makeQuery(id+"F0.imprint","IMPRINT",EDGE,{"derivedFrom":subQ11}),-1.0]])]});}
            var Q3;
            Q3=makeQuery(id+"F0.imprint","IMPRINT",FACE,{"disambiguationData":[TD([[makeQuery(id+"F0.imprint","IMPRINT",EDGE,{"derivedFrom":sQuery(id+"F0.wireOp",EDGE,"E38")}),-1.0]])]});
            var Q4;
            {var subQ3=sQuery(id+"F0.wireOp",EDGE,"E44");Q4=makeQuery(id+"F0.imprint","IMPRINT",FACE,{"disambiguationData":[TD([[makeQuery(id+"F0.imprint","IMPRINT",EDGE,{"derivedFrom":subQ3}),-1.0]])]});}
            var Q5;
            Q5=makeQuery(id+"F0.imprint","IMPRINT",FACE,{"disambiguationData":[TD([[makeQuery(id+"F0.imprint","IMPRINT",EDGE,{"derivedFrom":sQuery(id+"F0.wireOp",EDGE,"E0")}),-1.0]])]});
            extrude(context, id + "F3", {"entities" : qUnion([Q0, Q1, Q2, Q3, Q4, Q5]), "depth" : 500 * mm, "offsetDistance" : 25 * mm});
        }
    });
